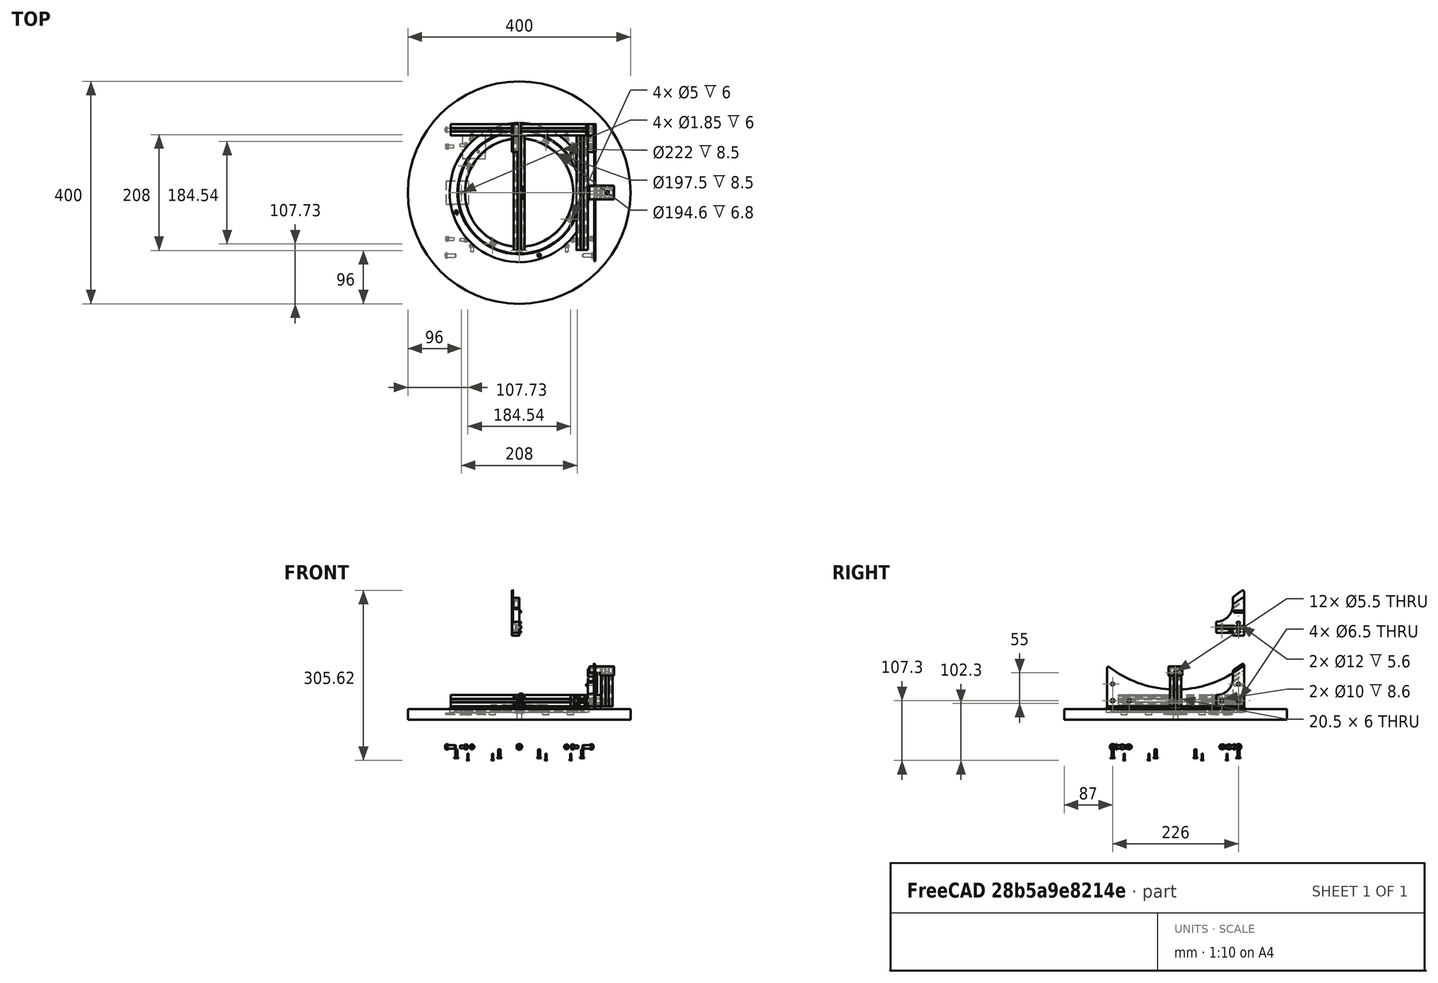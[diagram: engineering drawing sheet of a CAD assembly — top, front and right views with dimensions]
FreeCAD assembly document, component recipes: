
FREECAD ASSEMBLY — COMPONENT RECIPES ("Base")

This assembly document has 22 components, labeled P0..P21 below (a component is one placed body or linked part). 20 of them carry a construction recipe — the FreeCAD feature program that regenerates the part from scratch, quoted from this document or its linked companion documents; the rest are supplied as boundary geometry only. No exploded tour is included for this assembly.
NOTE — document 2 of 2 of this assembly tour. The two overview renders and the header above are repeated from document 1; the component sections below continue where the previous document stopped.
COMPONENT P13 — recipe-attached ("SideGuardPostA", modeled in this document).
Construction recipe (the document's own serialized feature program — sketch geometry with constraints, then the solid features built on it; lengths are millimeters unless a unit is written):

FEATURE [PartDesign::Plane] DatumPlane054  label="SideGuardPost_DatumPlane_Outer"
  AttachmentOffset = pos=(0,0,11) rot=(0,0,1;0rad)
  Length = 171.251
  MapMode = 5
  Placement = pos=(11,-2.4e-15,2.4e-15) rot=(0.57735,0.57735,0.57735;2.0944rad)
  ResizeMode = 0
  Support = -> [YZ_Plane125]
  Width = 114.566
  expr: .AttachmentOffset.Base.z = <<Common>>#<<Parameters>>.rail_width + 1
FEATURE [PartDesign::ShapeBinder] ShapeBinder015  label="SideGuardPost_ShapeBinder_Rocker"
  Support = -> [Binder]
  TraceSupport = false
FEATURE [PartDesign::Line] DatumLine004  label="SideGuardPost_DatumLine_RockerPivot"
  AttacherType = Attacher::AttachEngineLine
  Length = 20
  MapMode = 19
  Placement = pos=(0,0,215) rot=(0.57735,0.57735,0.57735;2.0944rad)
  ResizeMode = 0
  Support = -> [ShapeBinder015]
FEATURE [Sketcher::SketchObject] Sketch338  label="SideGuardPost_Block_Sketch"
  ExternalGeometry = -> [ShapeBinder015]
  FullyConstrained = true
  MapMode = 5
  Placement = pos=(0,0,0) rot=(0.57735,0.57735,0.57735;2.0944rad)
  Support = -> [YZ_Plane125]
  sketch-geometry (21):
    g0: LineSegment StartX=123 StartY=-14 StartZ=0 EndX=123 EndY=50.2697 EndZ=0
    g1: LineSegment StartX=73 StartY=-10 StartZ=0 EndX=73 EndY=10 EndZ=0
    g2: ArcOfCircle CenterX=120.5 CenterY=50.2697 CenterZ=0 NormalX=0 NormalY=0 NormalZ=1 AngleXU=0 Radius=2.5 StartAngle=1e-15 EndAngle=2.17123
    g3: Circle CenterX=113 CenterY=30 CenterZ=0 NormalX=0 NormalY=0 NormalZ=1 AngleXU=0 Radius=2.75
    g4: Circle CenterX=83 CenterY=0 CenterZ=0 NormalX=0 NormalY=0 NormalZ=1 AngleXU=0 Radius=2.75
    g5: Circle CenterX=113 CenterY=0 CenterZ=0 NormalX=0 NormalY=0 NormalZ=1 AngleXU=0 Radius=3.25
    g6: ArcOfCircle CenterX=73 CenterY=40 CenterZ=0 NormalX=0 NormalY=0 NormalZ=1 AngleXU=0 Radius=30 StartAngle=4.71239 EndAngle=6.28313
    g7: ArcOfCircle CenterX=105.5 CenterY=39.9981 CenterZ=0 NormalX=0 NormalY=0 NormalZ=1 AngleXU=0 Radius=2.5 StartAngle=2.17123 EndAngle=3.14153
    g8: LineSegment StartX=0 StartY=215 StartZ=0 EndX=113 EndY=49.9818 EndZ=0
    g9: LineSegment StartX=103 StartY=43.1341 StartZ=0 EndX=123 EndY=56.8295 EndZ=0
    g10: LineSegment StartX=113 StartY=49.9818 StartZ=0 EndX=113.847 EndY=48.7442 EndZ=0
    g11: LineSegment StartX=104.087 StartY=42.0608 StartZ=0 EndX=119.087 EndY=52.3324 EndZ=0
    g12: LineSegment StartX=103 StartY=39.9982 StartZ=0 EndX=103 EndY=43.1341 EndZ=0
    g13: LineSegment StartX=123 StartY=56.8295 StartZ=0 EndX=123 EndY=50.2697 EndZ=0
    g14: LineSegment StartX=122 StartY=-15 StartZ=0 EndX=104 EndY=-15 EndZ=0
    g15: LineSegment StartX=103 StartY=-14 StartZ=0 EndX=103 EndY=-6 EndZ=0
    g16: ArcOfCircle CenterX=104 CenterY=-14 CenterZ=0 NormalX=0 NormalY=0 NormalZ=1 AngleXU=0 Radius=1 StartAngle=3.14159 EndAngle=4.71239
    g17: ArcOfCircle CenterX=122 CenterY=-14 CenterZ=0 NormalX=0 NormalY=0 NormalZ=1 AngleXU=0 Radius=1 StartAngle=4.71239 EndAngle=6.28319
    g18: LineSegment StartX=93 StartY=-10 StartZ=0 EndX=73 EndY=-10 EndZ=0
    g19: LineSegment StartX=103 StartY=-6 StartZ=0 EndX=97 EndY=-6 EndZ=0
    g20: LineSegment StartX=97 StartY=-6 StartZ=0 EndX=93 EndY=-10 EndZ=0
  constraints (57):
    c: Vertical(g0)
    c: Coincident(g1,g18)
    c: Vertical(g1)
    c: Tangent(g0,g2) = -1.5708
    c: Coincident(g3,g-5)
    c: PointOnObject(g4,g-1)
    c: Coincident(g5,g-6)
    c: Diameter(g5) = 6.5
    c: Diameter(g3) = 5.5
    c: Equal(g3,g4)
    c: DistanceX(g4,g5) = 30
    c: DistanceX(g18,g4) = 10
    c: Radius(g2) = 2.5
    c: DistanceY(g1,g1) = 20
    c: Coincident(g6,g1)
    c: Equal(g7,g2)
    c: PointOnObject(g6,g1)
    c: Tangent(g7,g6) = 1.5708
    c: PointOnObject(g8,g-3)
    c: PointOnObject(g8,g-6)
    c: DistanceX(g9,g9) = 20
    c: PointOnObject(g8,g9)
    c: Coincident(g10,g8)
    c: PointOnObject(g10,g11)
    c: Parallel(g10,g8)
    c: Perpendicular(g11,g10)
    c: Tangent(g11,g2) = 1.5708
    c: Tangent(g11,g7) = 1.5708
    c: Distance(g10) = 1.5
    c: Coincident(g8,g-3)
    c: Coincident(g12,g6)
    c: Coincident(g12,g9)
    c: Vertical(g12)
    c: Coincident(g13,g9)
    c: Coincident(g13,g0)
    c: Vertical(g13)
    c: Perpendicular(g8,g9)
    c: Coincident(g15,g19)
    c: Horizontal(g14)
    c: Vertical(g15)
    c: Tangent(g15,g16) = 1.5708
    c: Tangent(g14,g16) = 1.5708
    c: Tangent(g0,g17) = -1.5708
    c: Tangent(g14,g17) = 1.5708
    c: Equal(g17,g16)
    c: Radius(g17) = 1
    c: DistanceX(g19,g5) = 10
    c: DistanceX(g5,g0) = 10
    c: Coincident(g20,g18)
    c: Horizontal(g18)
    c: Coincident(g19,g20)
    c: Horizontal(g19)
    c: DistanceY(g14,g18) = 5
    c: DistanceY(g18,g5) = 10
    c: DistanceX(g19,g19) = 6
    c: DistanceY(g20,g20) = 4
    c: Angle(g20,g19) = 2.35619
FEATURE [PartDesign::Pad] Pad093  label="SideGuardPost_Block"
  Direction = (1,-2e-16,3e-16)
  Length = 11
  Length2 = 10
  Placement = pos=(0,0,0) rot=(0.57735,0.57735,0.57735;2.0944rad)
  Profile = -> Sketch338
  ReferenceAxis = -> Sketch338 [N_Axis]
  Type = 0
  expr: Length = <<Common>>#<<Parameters>>.rail_width + 1
FEATURE [PartDesign::Plane] DatumPlane053  label="SideGuardPost_DatumPlane_Channel"
  AttachmentOffset = pos=(0,0,0) rot=(1,0,0;1.5708rad)
  Length = 67.8305
  MapMode = 13
  Placement = pos=(3.66667,114.087,48.9085) rot=(0,0.88459,-0.466369;3.14159rad)
  ResizeMode = 0
  Support = -> [Pad093]
  Width = 176.794
FEATURE [Sketcher::SketchObject] Sketch337  label="SideGuardPost_Plate_Sketch"
  ExternalGeometry = -> [ShapeBinder015,Sketch338]
  FullyConstrained = true
  MapMode = 5
  Placement = pos=(11,-2.4e-15,2.4e-15) rot=(0.57735,0.57735,0.57735;2.0944rad)
  Support = -> [DatumPlane054]
  expr: Constraints[2] = <<Common>>#<<Parameters>>.pri_fillet
  sketch-geometry (19):
    g0: LineSegment StartX=103 StartY=-10 StartZ=0 EndX=73 EndY=-10 EndZ=0
    g1: LineSegment StartX=0 StartY=215 StartZ=0 EndX=122.939 EndY=57.2468 EndZ=0
    g2: GeomPoint X=118.942 Y=65.7703 Z=0
    g3: Circle CenterX=113 CenterY=1.13e-14 CenterZ=0 NormalX=0 NormalY=0 NormalZ=1 AngleXU=0 Radius=3.25
    g4: ArcOfCircle CenterX=105.5 CenterY=52.9914 CenterZ=0 NormalX=0 NormalY=0 NormalZ=1 AngleXU=0 Radius=2.5 StartAngle=2.14801 EndAngle=3.14159
    g5: ArcOfCircle CenterX=120.5 CenterY=63.8154 CenterZ=0 NormalX=0 NormalY=0 NormalZ=1 AngleXU=0 Radius=2.5 StartAngle=-9e-16 EndAngle=2.24373
    g6: LineSegment StartX=123 StartY=63.8154 StartZ=0 EndX=123 EndY=-14 EndZ=0
    g7: LineSegment StartX=73 StartY=-10 StartZ=0 EndX=73 EndY=10 EndZ=0
    g8: ArcOfCircle CenterX=0 CenterY=215 CenterZ=0 NormalX=0 NormalY=0 NormalZ=1 AngleXU=0 Radius=190.831 StartAngle=5.28961 EndAngle=5.38532
    g9: LineSegment StartX=103 StartY=52.9914 StartZ=0 EndX=103 EndY=39.9982 EndZ=0
    g10: ArcOfCircle CenterX=73.0018 CenterY=39.9982 CenterZ=0 NormalX=0 NormalY=0 NormalZ=1 AngleXU=0 Radius=29.9982 StartAngle=4.71233 EndAngle=6.28319
    g11: GeomPoint X=117.303 Y=64.4786 Z=0
    g12: Circle CenterX=113 CenterY=70 CenterZ=0 NormalX=0 NormalY=0 NormalZ=1 AngleXU=0 Radius=6
    g13: LineSegment StartX=103 StartY=-10 StartZ=0 EndX=103 EndY=-14 EndZ=0
    g14: LineSegment StartX=104 StartY=-15 StartZ=0 EndX=122 EndY=-15 EndZ=0
    g15: ArcOfCircle CenterX=104 CenterY=-14 CenterZ=0 NormalX=0 NormalY=0 NormalZ=1 AngleXU=0 Radius=1 StartAngle=3.14159 EndAngle=4.71239
    g16: ArcOfCircle CenterX=122 CenterY=-14 CenterZ=0 NormalX=0 NormalY=0 NormalZ=1 AngleXU=0 Radius=1 StartAngle=4.71239 EndAngle=6.28319
    g17: LineSegment StartX=122 StartY=-14 StartZ=0 EndX=122 EndY=-15 EndZ=0
    g18: LineSegment StartX=104 StartY=-14 StartZ=0 EndX=104 EndY=-15 EndZ=0
  constraints (44):
    c: Diameter(g3) = 6.5
    c: Equal(g5,g4)
    c: Radius(g5) = 2.5
    c: Vertical(g6)
    c: Tangent(g5,g6) = 1.5708
    c: Coincident(g8,g1)
    c: Tangent(g8,g5) = 1.5708
    c: Tangent(g8,g4) = 1.5708
    c: PointOnObject(g1,g-3)
    c: Coincident(g2,g5)
    c: Vertical(g9)
    c: Tangent(g9,g4) = -1.5708
    c: Tangent(g10,g9) = 1.5708
    c: Coincident(g8,g-3)
    c: Coincident(g3,g-4)
    c: PointOnObject(g-4,g1)
    c: PointOnObject(g11,g1)
    c: PointOnObject(g11,g8)
    c: Distance(g11,g-4) = 7
    c: Coincident(g12,g-4)
    c: Diameter(g12) = 12
    c: Horizontal(g14)
    c: Coincident(g0,g13)
    c: Coincident(g7,g0)
    c: Coincident(g7,g10)
    c: Coincident(g7,g-5)
    c: Coincident(g0,g-5)
    c: Coincident(g15,g13)
    c: Coincident(g16,g-6)
    c: Coincident(g16,g6)
    c: Coincident(g14,g16)
    c: Coincident(g15,g14)
    c: Equal(g15,g16)
    c: Coincident(g6,g-6)
    c: Coincident(g17,g16)
    c: Coincident(g17,g14)
    c: Coincident(g18,g15)
    c: Coincident(g18,g14)
    c: Vertical(g18)
    c: Vertical(g17)
    c: Coincident(g9,g-7)
    c: Horizontal(g0)
    c: Vertical(g13)
    c: Coincident(g13,g-8)
FEATURE [PartDesign::Pad] Pad094  label="SideGuardPost_Plate"
  BaseFeature = -> Pad093
  Direction = (1,-1e-16,1e-16)
  Length = 2
  Length2 = 10
  Placement = pos=(0,0,0) rot=(0.57735,0.57735,0.57735;2.0944rad)
  Profile = -> Sketch337
  ReferenceAxis = -> Sketch337 [N_Axis]
  Type = 0
  expr: Length = Common#<<Parameters>>.rocker_plate
FEATURE [Sketcher::SketchObject] Sketch339  label="SideGuardPost_SideRail_Sketch"
  ExternalGeometry = -> [ShapeBinder015]
  FullyConstrained = true
  MapMode = 5
  Placement = pos=(0,0,0) rot=(-0.57735,0.57735,0.57735;4.18879rad)
  Support = -> [YZ_Plane125]
  sketch-geometry (22):
    g0: LineSegment StartX=-88 StartY=3 StartZ=0 EndX=-106 EndY=3 EndZ=0
    g1: LineSegment StartX=-106 StartY=3 StartZ=0 EndX=-106 EndY=-3 EndZ=0
    g2: LineSegment StartX=-106 StartY=-3 StartZ=0 EndX=-88 EndY=-3 EndZ=0
    g3: LineSegment StartX=-88 StartY=-3 StartZ=0 EndX=-88 EndY=3 EndZ=0
    g4: LineSegment StartX=-73 StartY=3 StartZ=0 EndX=-78 EndY=3 EndZ=0
    g5: LineSegment StartX=-78 StartY=3 StartZ=0 EndX=-78 EndY=-3 EndZ=0
    g6: LineSegment StartX=-78 StartY=-3 StartZ=0 EndX=-73 EndY=-3 EndZ=0
    g7: LineSegment StartX=-73 StartY=-3 StartZ=0 EndX=-73 EndY=3 EndZ=0
    g8: LineSegment StartX=-88 StartY=0 StartZ=0 EndX=-83 EndY=0 EndZ=0
    g9: LineSegment StartX=-83 StartY=0 StartZ=0 EndX=-78 EndY=0 EndZ=0
    g10: LineSegment StartX=-123 StartY=3 StartZ=0 EndX=-120 EndY=3 EndZ=0
    g11: LineSegment StartX=-120 StartY=3 StartZ=0 EndX=-120 EndY=-3 EndZ=0
    g12: LineSegment StartX=-120 StartY=-3 StartZ=0 EndX=-123 EndY=-3 EndZ=0
    g13: LineSegment StartX=-123 StartY=-3 StartZ=0 EndX=-123 EndY=3 EndZ=0
    g14: LineSegment StartX=-116 StartY=10 StartZ=0 EndX=-110 EndY=10 EndZ=0
    g15: LineSegment StartX=-110 StartY=10 StartZ=0 EndX=-110 EndY=7 EndZ=0
    g16: LineSegment StartX=-110 StartY=7 StartZ=0 EndX=-116 EndY=7 EndZ=0
    g17: LineSegment StartX=-116 StartY=7 StartZ=0 EndX=-116 EndY=10 EndZ=0
    g18: LineSegment StartX=-116 StartY=-7 StartZ=0 EndX=-110 EndY=-7 EndZ=0
    g19: LineSegment StartX=-110 StartY=-7 StartZ=0 EndX=-110 EndY=-10 EndZ=0
    g20: LineSegment StartX=-110 StartY=-10 StartZ=0 EndX=-116 EndY=-10 EndZ=0
    g21: LineSegment StartX=-116 StartY=-10 StartZ=0 EndX=-116 EndY=-7 EndZ=0
  constraints (63):
    c: DistanceX(g-3,g8) = 30
    c: Coincident(g0,g1)
    c: Coincident(g2,g1)
    c: Coincident(g3,g2)
    c: Coincident(g0,g3)
    c: PointOnObject(g8,g3)
    c: Coincident(g8,g9)
    c: Coincident(g5,g6)
    c: Coincident(g6,g7)
    c: Coincident(g4,g7)
    c: Coincident(g4,g5)
    c: Equal(g8,g9)
    c: PointOnObject(g9,g5)
    c: Symmetric(g4,g6,g-1)
    c: DistanceY(g7,g7) = 6
    c: Vertical(g3)
    c: Vertical(g1)
    c: Coincident(g10,g11)
    c: Coincident(g11,g12)
    c: Coincident(g12,g13)
    c: Coincident(g13,g10)
    c: Horizontal(g10)
    c: Horizontal(g12)
    c: Vertical(g11)
    c: Vertical(g13)
    c: Coincident(g14,g15)
    c: Coincident(g15,g16)
    c: Coincident(g16,g17)
    c: Coincident(g17,g14)
    c: Horizontal(g16)
    c: Vertical(g15)
    c: Vertical(g17)
    c: Coincident(g18,g19)
    c: Coincident(g19,g20)
    c: Coincident(g20,g21)
    c: Coincident(g21,g18)
    c: Horizontal(g18)
    c: Horizontal(g20)
    c: Vertical(g19)
    c: Vertical(g21)
    c: Horizontal(g2)
    c: Horizontal(g0)
    c: Horizontal(g8)
    c: Horizontal(g9)
    c: PointOnObject(g9,g-1)
    c: Vertical(g5)
    c: Horizontal(g4)
    c: Horizontal(g6)
    c: Equal(g14,g13)
    c: Equal(g13,g20)
    c: Equal(g20,g3)
    c: Equal(g3,g7)
    c: DistanceX(g8,g4) = 10
    c: Equal(g12,g19)
    c: Equal(g19,g17)
    c: Symmetric(g14,g14,g-4)
    c: Symmetric(g14,g19,g-1)
    c: DistanceY(g20,g14) = 20
    c: PointOnObject(g4,g0)
    c: DistanceX(g10,g-4) = 10
    c: DistanceX(g8,g9) = 10
    c: Symmetric(g0,g10,g-4)
    c: DistanceY(g15,g15) = 3
FEATURE [PartDesign::Pad] Pad095  label="SideGuardPost_SideRail"
  BaseFeature = -> Pad094
  Direction = (-1,2e-16,-3e-16)
  Length = 3
  Length2 = 10
  Placement = pos=(0,0,0) rot=(0.57735,0.57735,0.57735;2.0944rad)
  Profile = -> Sketch339
  ReferenceAxis = -> Sketch339 [N_Axis]
  Type = 0
FEATURE [Sketcher::SketchObject] Sketch340  label="SideGuardPost_SideBolt_Sketch"
  AttachmentOffset = pos=(0,0,2) rot=(0,0,1;0rad)
  ExternalGeometry = -> [ShapeBinder015]
  FullyConstrained = true
  MapMode = 5
  Placement = pos=(13,-2.7e-15,2.7e-15) rot=(0.57735,0.57735,0.57735;2.0944rad)
  Support = -> [DatumPlane054]
  expr: .AttachmentOffset.Base.z = <<Common>>#<<Parameters>>.rocker_plate
  sketch-geometry (2):
    g0: Circle CenterX=83 CenterY=0 CenterZ=0 NormalX=0 NormalY=0 NormalZ=1 AngleXU=0 Radius=2.75
    g1: Circle CenterX=113 CenterY=0 CenterZ=0 NormalX=0 NormalY=0 NormalZ=1 AngleXU=0 Radius=3.25
  constraints (5):
    c: PointOnObject(g0,g-1)
    c: Diameter(g0) = 5.5
    c: Coincident(g1,g-3)
    c: Diameter(g1) = 6.5
    c: DistanceX(g0,g1) = 30
FEATURE [Sketcher::SketchObject] Sketch341  label="SideGuardPost_CounterBoreSide_Sketch"
  AttachmentOffset = pos=(0,0,2) rot=(0,0,1;0rad)
  ExternalGeometry = -> [Sketch340]
  FullyConstrained = true
  MapMode = 5
  Placement = pos=(13,-2.7e-15,2.7e-15) rot=(0.57735,0.57735,0.57735;2.0944rad)
  Support = -> [DatumPlane054]
  expr: .AttachmentOffset.Base.z = <<Common>>#<<Parameters>>.rocker_plate
  sketch-geometry (1):
    g0: Circle CenterX=83 CenterY=-9.3e-15 CenterZ=0 NormalX=0 NormalY=0 NormalZ=1 AngleXU=0 Radius=5
  constraints (2):
    c: Diameter(g0) = 10
    c: Coincident(g0,g-3)
FEATURE [Sketcher::SketchObject] Sketch342  label="SideGuardPost_CBSSupport_Sketch"
  AttachmentOffset = pos=(0,0,-7) rot=(0,0,1;0rad)
  ExternalGeometry = -> [Sketch340,Sketch341]
  FullyConstrained = true
  MapMode = 5
  Placement = pos=(4,-1.7e-15,1.7e-15) rot=(0.57735,0.57735,0.57735;2.0944rad)
  Support = -> [DatumPlane054]
  expr: .AttachmentOffset.Base.z = -(<<Common>>#<<Parameters>>.rail_width + 1 - 4)
  sketch-geometry (12):
    g0: LineSegment StartX=78.8242 StartY=2.75 StartZ=0 EndX=87.1758 EndY=2.75 EndZ=0
    g1: LineSegment StartX=87.4695 StartY=2.24137 StartZ=0 EndX=83.2937 EndY=-4.99137 EndZ=0
    g2: LineSegment StartX=82.7063 StartY=-4.99137 StartZ=0 EndX=78.5305 EndY=2.24137 EndZ=0
    g3: ArcOfCircle CenterX=83 CenterY=-9.2e-15 CenterZ=0 NormalX=0 NormalY=0 NormalZ=1 AngleXU=0 Radius=5 StartAngle=2.55923 EndAngle=2.67676
    g4: ArcOfCircle CenterX=83 CenterY=-9.2e-15 CenterZ=0 NormalX=0 NormalY=0 NormalZ=1 AngleXU=0 Radius=5 StartAngle=0.464833 EndAngle=0.582364
    g5: ArcOfCircle CenterX=83 CenterY=-9.2e-15 CenterZ=0 NormalX=0 NormalY=0 NormalZ=1 AngleXU=0 Radius=5 StartAngle=4.65362 EndAngle=4.77115
    g6: LineSegment StartX=83 StartY=-9.2e-15 StartZ=0 EndX=83 EndY=2.75 EndZ=0
    g7: LineSegment StartX=83 StartY=-9.2e-15 StartZ=0 EndX=85.3816 EndY=-1.375 EndZ=0
    g8: LineSegment StartX=83 StartY=-9.2e-15 StartZ=0 EndX=80.6184 EndY=-1.375 EndZ=0
    g9: LineSegment StartX=85.3816 StartY=-1.375 StartZ=0 EndX=80.6184 EndY=-1.375 EndZ=0
    g10: LineSegment StartX=80.6184 StartY=-1.375 StartZ=0 EndX=83 EndY=2.75 EndZ=0
    g11: LineSegment StartX=83 StartY=2.75 StartZ=0 EndX=85.3816 EndY=-1.375 EndZ=0
  constraints (33):
    c: Horizontal(g0)
    c: Coincident(g3,g2)
    c: Coincident(g3,g0)
    c: Coincident(g4,g3)
    c: Coincident(g4,g0)
    c: Coincident(g4,g1)
    c: Coincident(g5,g3)
    c: Coincident(g5,g1)
    c: Coincident(g5,g2)
    c: Coincident(g6,g3)
    c: PointOnObject(g6,g0)
    c: Vertical(g6)
    c: Coincident(g7,g3)
    c: Coincident(g8,g3)
    c: PointOnObject(g8,g2)
    c: Coincident(g9,g7)
    c: Coincident(g9,g8)
    c: Coincident(g10,g8)
    c: Coincident(g10,g6)
    c: Coincident(g11,g6)
    c: Coincident(g11,g7)
    c: Horizontal(g9)
    c: Equal(g11,g9)
    c: Perpendicular(g2,g8)
    c: Perpendicular(g1,g7)
    c: Equal(g10,g11)
    c: PointOnObject(g7,g1)
    c: PointOnObject(g0,g-4)
    c: PointOnObject(g2,g-4)
    c: PointOnObject(g0,g-4)
    c: PointOnObject(g6,g-3)
    c: PointOnObject(g7,g-3)
    c: Coincident(g3,g-4)
FEATURE [Sketcher::SketchObject] Sketch343  label="SideGuardPost_Channel_Sketch"
  ExternalGeometry = -> [Pad093]
  FullyConstrained = true
  MapMode = 5
  Placement = pos=(3.66667,114.087,48.9085) rot=(0,0.88459,-0.466369;3.14159rad)
  Support = -> [DatumPlane053]
  sketch-geometry (6):
    g0: LineSegment StartX=-4.63333 StartY=6.6 StartZ=0 EndX=0.966667 EndY=6.6 EndZ=0
    g1: LineSegment StartX=0.966667 StartY=6.6 StartZ=0 EndX=0.966667 EndY=5 EndZ=0
    g2: LineSegment StartX=0.966667 StartY=5 StartZ=0 EndX=-4.63333 EndY=5 EndZ=0
    g3: LineSegment StartX=-4.63333 StartY=5 StartZ=0 EndX=-4.63333 EndY=6.6 EndZ=0
    g4: LineSegment StartX=-4.63333 StartY=5 StartZ=0 EndX=-7.33333 EndY=5 EndZ=0
    g5: LineSegment StartX=0.966667 StartY=5 StartZ=0 EndX=3.66667 EndY=5 EndZ=0
  constraints (18):
    c: Coincident(g0,g1)
    c: Coincident(g1,g2)
    c: Coincident(g2,g3)
    c: Coincident(g3,g0)
    c: Horizontal(g0)
    c: Horizontal(g2)
    c: Vertical(g1)
    c: Vertical(g3)
    c: Coincident(g4,g2)
    c: Horizontal(g4)
    c: Coincident(g5,g1)
    c: Horizontal(g5)
    c: Equal(g4,g5)
    c: DistanceX(g2,g2) = 5.6
    c: DistanceY(g1,g1) = 1.6
    c: DistanceY(g-1,g1) = 5
    c: PointOnObject(g4,g-4)
    c: PointOnObject(g5,g-5)
FEATURE [Sketcher::SketchObject] Sketch344  label="SideGuardPost_UpperCatch_Sketch"
  ExternalGeometry = -> [ShapeBinder015]
  FullyConstrained = true
  MapMode = 5
  Placement = pos=(0,0,0) rot=(0.57735,0.57735,0.57735;2.0944rad)
  Support = -> [YZ_Plane125]
  sketch-geometry (4):
    g0: LineSegment StartX=105 StartY=30 StartZ=0 EndX=121 EndY=30 EndZ=0
    g1: LineSegment StartX=121 StartY=30 StartZ=0 EndX=121 EndY=26 EndZ=0
    g2: LineSegment StartX=121 StartY=26 StartZ=0 EndX=105 EndY=26 EndZ=0
    g3: LineSegment StartX=105 StartY=26 StartZ=0 EndX=105 EndY=30 EndZ=0
  constraints (11):
    c: Coincident(g0,g1)
    c: Coincident(g1,g2)
    c: Coincident(g2,g3)
    c: Coincident(g3,g0)
    c: Horizontal(g2)
    c: Vertical(g1)
    c: Vertical(g3)
    c: Symmetric(g0,g0,g-4)
    c: DistanceY(g1,g1) = 4
    c: DistanceX(g2,g2) = 16
    c: PointOnObject(g-3,g0)
FEATURE [PartDesign::Pad] Pad096  label="SideGuardPost_Catch"
  BaseFeature = -> Pad095
  Direction = (1,-2e-16,3e-16)
  Length = 3
  Length2 = 10
  Placement = pos=(0,0,0) rot=(0.57735,0.57735,0.57735;2.0944rad)
  Profile = -> Sketch344
  ReferenceAxis = -> Sketch344 [N_Axis]
  Reversed = true
  Type = 0
FEATURE [Sketcher::SketchObject] Sketch347  label="SideGuardPost_CornerBolt_Sketch"
  AttachmentOffset = pos=(0,0,2) rot=(0,0,1;0rad)
  ExternalGeometry = -> [ShapeBinder015]
  FullyConstrained = true
  MapMode = 5
  Placement = pos=(13,-2.7e-15,2.7e-15) rot=(0.57735,0.57735,0.57735;2.0944rad)
  Support = -> [DatumPlane054]
  expr: .AttachmentOffset.Base.z = <<Common>>#<<Parameters>>.rocker_plate
  sketch-geometry (1):
    g0: Circle CenterX=113 CenterY=0 CenterZ=0 NormalX=0 NormalY=0 NormalZ=1 AngleXU=0 Radius=3.25
  constraints (2):
    c: Coincident(g0,g-3)
    c: Diameter(g0) = 6.5
FEATURE [Sketcher::SketchObject] Sketch345  label="SideGuardPost_CounterBoreCorner_Sketch"
  AttachmentOffset = pos=(0,0,2) rot=(0,0,1;0rad)
  ExternalGeometry = -> [Sketch347]
  FullyConstrained = true
  MapMode = 5
  Placement = pos=(13,-2.7e-15,2.7e-15) rot=(0.57735,0.57735,0.57735;2.0944rad)
  Support = -> [DatumPlane054]
  expr: .AttachmentOffset.Base.z = <<Common>>#<<Parameters>>.rocker_plate
  sketch-geometry (1):
    g0: Circle CenterX=113 CenterY=-1.25e-14 CenterZ=0 NormalX=0 NormalY=0 NormalZ=1 AngleXU=0 Radius=6
  constraints (2):
    c: Diameter(g0) = 12
    c: Coincident(g0,g-3)
FEATURE [Sketcher::SketchObject] Sketch346  label="SideGuardPost_CBCSupport_Sketch"
  AttachmentOffset = pos=(0,0,-4) rot=(0,0,1;0rad)
  ExternalGeometry = -> [Sketch347,Sketch345]
  FullyConstrained = true
  MapMode = 5
  Placement = pos=(7,-2e-15,2e-15) rot=(0.57735,0.57735,0.57735;2.0944rad)
  Support = -> [DatumPlane054]
  expr: .AttachmentOffset.Base.z = <<Common>>#<<Parameters>>.rocker_plate - 6
  sketch-geometry (12):
    g0: LineSegment StartX=107.956 StartY=3.25 StartZ=0 EndX=118.044 EndY=3.25 EndZ=0
    g1: LineSegment StartX=118.336 StartY=2.74285 StartZ=0 EndX=113.293 EndY=-5.99285 EndZ=0
    g2: LineSegment StartX=112.707 StartY=-5.99285 StartZ=0 EndX=107.664 EndY=2.74285 EndZ=0
    g3: ArcOfCircle CenterX=113 CenterY=-2.51e-14 CenterZ=0 NormalX=0 NormalY=0 NormalZ=1 AngleXU=0 Radius=6 StartAngle=2.56917 EndAngle=2.66681
    g4: ArcOfCircle CenterX=113 CenterY=-2.51e-14 CenterZ=0 NormalX=0 NormalY=0 NormalZ=1 AngleXU=0 Radius=6 StartAngle=0.474779 EndAngle=0.572419
    g5: ArcOfCircle CenterX=113 CenterY=-2.51e-14 CenterZ=0 NormalX=0 NormalY=0 NormalZ=1 AngleXU=0 Radius=6 StartAngle=4.66357 EndAngle=4.76121
    g6: LineSegment StartX=113 StartY=-2.51e-14 StartZ=0 EndX=113 EndY=3.25 EndZ=0
    g7: LineSegment StartX=113 StartY=-2.51e-14 StartZ=0 EndX=110.185 EndY=-1.625 EndZ=0
    g8: LineSegment StartX=113 StartY=-2.51e-14 StartZ=0 EndX=115.815 EndY=-1.625 EndZ=0
    g9: LineSegment StartX=115.815 StartY=-1.625 StartZ=0 EndX=110.185 EndY=-1.625 EndZ=0
    g10: LineSegment StartX=110.185 StartY=-1.625 StartZ=0 EndX=113 EndY=3.25 EndZ=0
    g11: LineSegment StartX=113 StartY=3.25 StartZ=0 EndX=115.815 EndY=-1.625 EndZ=0
  constraints (33):
    c: Horizontal(g0)
    c: Coincident(g3,g2)
    c: Coincident(g3,g0)
    c: Coincident(g4,g3)
    c: Coincident(g4,g0)
    c: Coincident(g4,g1)
    c: Coincident(g5,g3)
    c: Coincident(g5,g1)
    c: Coincident(g5,g2)
    c: Coincident(g6,g3)
    c: PointOnObject(g6,g0)
    c: Vertical(g6)
    c: Coincident(g7,g3)
    c: PointOnObject(g7,g2)
    c: Coincident(g8,g3)
    c: PointOnObject(g8,g1)
    c: Coincident(g9,g8)
    c: Coincident(g9,g7)
    c: Perpendicular(g2,g7)
    c: Perpendicular(g1,g8)
    c: Coincident(g10,g7)
    c: Coincident(g10,g6)
    c: Coincident(g11,g6)
    c: Coincident(g11,g8)
    c: Equal(g10,g11)
    c: Equal(g11,g9)
    c: Horizontal(g9)
    c: PointOnObject(g0,g-4)
    c: PointOnObject(g2,g-4)
    c: PointOnObject(g1,g-4)
    c: Coincident(g3,g-4)
    c: PointOnObject(g8,g-3)
    c: PointOnObject(g6,g-3)
FEATURE [PartDesign::Pocket] Pocket196  label="SideGuardPost_Channel"
  BaseFeature = -> Pad096
  Direction = (0,0.825091,0.565)
  Length = 5
  Length2 = 5
  Midplane = true
  Placement = pos=(0,0,0) rot=(0.57735,0.57735,0.57735;2.0944rad)
  Profile = -> Sketch343
  ReferenceAxis = -> Sketch343 [N_Axis]
  Type = 1
FEATURE [Sketcher::SketchObject] Sketch348  label="SideGuardPost_LowerChannel_Sketch"
  AttachmentOffset = pos=(0,0,123) rot=(0,0,1;0rad)
  FullyConstrained = true
  MapMode = 5
  Placement = pos=(0,123,2.73e-14) rot=(0,0.707107,0.707107;3.14159rad)
  Support = -> [XZ_Plane124]
  expr: .AttachmentOffset.Base.z = <<Common>>#<<Parameters>>.boxsize_y / 2
  expr: Constraints[12] = <<Common>>#<<Parameters>>.rail_width + 1
  sketch-geometry (7):
    g0: LineSegment StartX=-2.7 StartY=-8.4 StartZ=0 EndX=-8.3 EndY=-8.4 EndZ=0
    g1: LineSegment StartX=-8.3 StartY=-8.4 StartZ=0 EndX=-8.3 EndY=-10 EndZ=0
    g2: LineSegment StartX=-8.3 StartY=-10 StartZ=0 EndX=-2.7 EndY=-10 EndZ=0
    g3: LineSegment StartX=-2.7 StartY=-10 StartZ=0 EndX=-2.7 EndY=-8.4 EndZ=0
    g4: LineSegment StartX=-11 StartY=0 StartZ=0 EndX=-11 EndY=-10 EndZ=0
    g5: LineSegment StartX=-11 StartY=-10 StartZ=0 EndX=-8.3 EndY=-10 EndZ=0
    g6: LineSegment StartX=-2.7 StartY=-10 StartZ=0 EndX=0 EndY=-10 EndZ=0
  constraints (21):
    c: Coincident(g0,g1)
    c: Coincident(g1,g2)
    c: Coincident(g2,g3)
    c: Coincident(g3,g0)
    c: Horizontal(g0)
    c: Horizontal(g2)
    c: Vertical(g1)
    c: Vertical(g3)
    c: PointOnObject(g4,g-1)
    c: Vertical(g4)
    c: DistanceX(g2,g2) = 5.6
    c: DistanceY(g1,g1) = 1.6
    c: DistanceX(g4,g-1) = 11
    c: Coincident(g5,g4)
    c: Coincident(g5,g1)
    c: Coincident(g6,g2)
    c: PointOnObject(g6,g-2)
    c: Horizontal(g6)
    c: Horizontal(g5)
    c: Equal(g5,g6)
    c: DistanceY(g6,g-1) = 10
FEATURE [PartDesign::Pocket] Pocket197  label="SideGuardPost_LowerChannel"
  BaseFeature = -> Pocket196
  Direction = (0,-1,-2e-16)
  Length = 5
  Length2 = 5
  Placement = pos=(0,0,0) rot=(0.57735,0.57735,0.57735;2.0944rad)
  Profile = -> Sketch348
  ReferenceAxis = -> Sketch348 [N_Axis]
  Type = 2
FEATURE [PartDesign::Pocket] Pocket198  label="SideGuardPost_CornerBolt"
  BaseFeature = -> Pocket197
  Direction = (-1,1e-16,-1e-16)
  Length = 5
  Length2 = 5
  Placement = pos=(0,0,0) rot=(0.57735,0.57735,0.57735;2.0944rad)
  Profile = -> Sketch347
  ReferenceAxis = -> Sketch347 [N_Axis]
  Type = 1
FEATURE [PartDesign::Pocket] Pocket199  label="SideGuardPost_SideBolt"
  BaseFeature = -> Pocket198
  Direction = (-1,1e-16,-1e-16)
  Length = 5
  Length2 = 5
  Placement = pos=(0,0,0) rot=(0.57735,0.57735,0.57735;2.0944rad)
  Profile = -> Sketch340
  ReferenceAxis = -> Sketch340 [N_Axis]
  Type = 1
FEATURE [PartDesign::Pocket] Pocket200  label="SideGuardPost_CounterBoreCorner"
  BaseFeature = -> Pocket199
  Direction = (-1,1e-16,-1e-16)
  Length = 6
  Length2 = 5
  Placement = pos=(0,0,0) rot=(0.57735,0.57735,0.57735;2.0944rad)
  Profile = -> Sketch345
  ReferenceAxis = -> Sketch345 [N_Axis]
  Type = 0
FEATURE [PartDesign::Pocket] Pocket201  label="SideGuardPost_CounterBoreSide"
  BaseFeature = -> Pocket200
  Direction = (-1,1e-16,-1e-16)
  Length = 9
  Length2 = 5
  Placement = pos=(0,0,0) rot=(0.57735,0.57735,0.57735;2.0944rad)
  Profile = -> Sketch341
  ReferenceAxis = -> Sketch341 [N_Axis]
  Type = 0
  expr: Length = <<Common>>#<<Parameters>>.rail_width + 1 + <<Common>>#<<Parameters>>.rocker_plate - 4
FEATURE [PartDesign::Pocket] Pocket202  label="SideGuardPost_CBCSupport"
  BaseFeature = -> Pocket201
  Direction = (-1,1e-16,-1e-16)
  Length = 0.2
  Length2 = 5
  Placement = pos=(0,0,0) rot=(0.57735,0.57735,0.57735;2.0944rad)
  Profile = -> Sketch346
  ReferenceAxis = -> Sketch346 [N_Axis]
  Type = 0
FEATURE [PartDesign::Pocket] Pocket203  label="SideGuardPost_CBSSupport"
  BaseFeature = -> Pocket202
  Direction = (-1,1e-16,-1e-16)
  Length = 0.2
  Length2 = 5
  Placement = pos=(0,0,0) rot=(0.57735,0.57735,0.57735;2.0944rad)
  Profile = -> Sketch342
  ReferenceAxis = -> Sketch342 [N_Axis]
  Type = 0
FEATURE [PartDesign::Chamfer] Chamfer004  label="SideGuardPost_Chamfer"
  Angle = 45
  Base = -> Pocket203 [Face51]
  BaseFeature = -> Pocket203
  ChamferType = 0
  FlipDirection = false
  Placement = pos=(0,0,0) rot=(0.57735,0.57735,0.57735;2.0944rad)
  Size = 0.4
  Size2 = 1
  SupportTransform = false
  UseAllEdges = false
FEATURE [PartDesign::CoordinateSystem] Local_CS258  label="LCS_SideGuardPostA_Corner"
  AttacherType = Attacher::AttachEngine3D
  MapMode = 11
  Placement = pos=(1.78e-14,113,-3.93e-14) rot=(0.707107,0,0.707107;3.14159rad)
  Support = -> [Chamfer004]
FEATURE [PartDesign::CoordinateSystem] Local_CS259  label="LCS_SideGuardPostA_Side"
  AttacherType = Attacher::AttachEngine3D
  AttachmentOffset = pos=(0,0,0) rot=(0,0,1;1.5708rad)
  MapMode = 11
  Placement = pos=(-3.55e-14,83,-2.93e-14) rot=(0.57735,-0.57735,0.57735;4.18879rad)
  Support = -> [Chamfer004]
FEATURE [PartDesign::Body] Body022070  label="SideGuardPostA"
  Group = -> [ShapeBinder015,Sketch338,Sketch339,Sketch337,DatumLine004,DatumPlane053,Pad093,Pad094,Pad095,Sketch340,Sketch341,Sketch342,DatumPlane054,Sketch343,Sketch344,Sketch345,Sketch346,Pad096,Sketch347,Pocket196,Sketch348,Pocket197,Pocket198,Pocket199,Pocket200,Pocket201,Pocket202,Pocket203,Chamfer004,Local_CS258,Local_CS259]
  Origin = -> Origin124
  Placement = pos=(123,0,-132) rot=(0,0,1;0rad)
  Tip = -> Chamfer004
  expr: .Placement.Base.x = <<Common>>#<<Parameters>>.boxsize_x / 2
  expr: .Placement.Base.z = <<Common>>#<<Parameters>>.datum_azbase
COMPONENT P14 — geometry summary ("SideGuardPostB"; no construction recipe available for this part):
  bounding box: 81.3 x 50.0 x 16.0 mm
  tessellated surface: 3,632 triangles
  volume: 25453 mm^3 (39% of its bounding box)
COMPONENT P15 — recipe-attached ("BaseWheelBlockSB", modeled in this document).
Construction recipe (the document's own serialized feature program — sketch geometry with constraints, then the solid features built on it; lengths are millimeters unless a unit is written):

FEATURE [Sketcher::SketchObject] Sketch350  label="BaseWheelBlockSB_Body_Sketch"
  FullyConstrained = true
  MapMode = 5
  Support = -> [XY_Plane128]
  expr: Constraints[22] = <<Common>>#<<Parameters>>.bolt_y - 10 - 30
  expr: Constraints[32] = <<Common>>#<<Parameters>>.bolt_x - 10
  sketch-geometry (23):
    g0: ArcOfCircle CenterX=0 CenterY=0 CenterZ=0 NormalX=0 NormalY=0 NormalZ=1 AngleXU=0 Radius=104.75 StartAngle=0 EndAngle=1.5708
    g1: LineSegment StartX=88.1276 StartY=63.0542 StartZ=0 EndX=99.4503 EndY=43.0343 EndZ=0
    g2: LineSegment StartX=99.4503 StartY=43.0343 StartZ=0 EndX=93.3573 EndY=39.5883 EndZ=0
    g3: LineSegment StartX=93.3573 StartY=39.5883 StartZ=0 EndX=82.0346 EndY=59.6082 EndZ=0
    g4: LineSegment StartX=82.0346 StartY=59.6082 StartZ=0 EndX=88.1276 EndY=63.0542 EndZ=0
    g5: LineSegment StartX=91.1777 StartY=51.5674 StartZ=0 EndX=0 EndY=0 EndZ=0
    g6: LineSegment StartX=92 StartY=73 StartZ=0 EndX=103 EndY=73 EndZ=0
    g7: LineSegment StartX=103 StartY=73 StartZ=0 EndX=103 EndY=46.5731 EndZ=0
    g8: LineSegment StartX=92 StartY=58.2387 StartZ=0 EndX=92 EndY=73 EndZ=0
    g9: GeomPoint X=93.789 Y=53.0443 Z=0
    g10: GeomPoint X=94.6594 Y=53.5366 Z=0
    g11: LineSegment StartX=98.5977 StartY=46.5731 StartZ=0 EndX=92 EndY=58.2387 EndZ=0
    g12: LineSegment StartX=98.5977 StartY=46.5731 StartZ=0 EndX=103 EndY=46.5731 EndZ=0
    g13: GeomPoint X=87.6959 Y=49.5982 Z=0
    g14: LineSegment StartX=103 StartY=68 StartZ=0 EndX=99 EndY=68 EndZ=0
    g15: LineSegment StartX=99 StartY=68 StartZ=0 EndX=99 EndY=70.5 EndZ=0
    g16: LineSegment StartX=99 StartY=70.5 StartZ=0 EndX=85.0654 EndY=70.5 EndZ=0
    g17: LineSegment StartX=103 StartY=63 StartZ=0 EndX=99 EndY=63 EndZ=0
    g18: LineSegment StartX=99 StartY=63 StartZ=0 EndX=99 EndY=60.5 EndZ=0
    g19: LineSegment StartX=99 StartY=60.5 StartZ=0 EndX=90.7211 EndY=60.5 EndZ=0
    g20: LineSegment StartX=96.1363 StartY=50.9253 StartZ=0 EndX=100.488 EndY=53.3867 EndZ=0
    g21: LineSegment StartX=93.1825 StartY=56.1478 StartZ=0 EndX=97.5347 EndY=58.6093 EndZ=0
    g22: LineSegment StartX=97.5347 StartY=58.6093 StartZ=0 EndX=100.488 EndY=53.3867 EndZ=0
  constraints (70):
    c: Coincident(g0,g-1)
    c: PointOnObject(g0,g-2)
    c: PointOnObject(g0,g-1)
    c: DistanceY(g0) = 104.75
    c: Coincident(g2,g1)
    c: Coincident(g3,g2)
    c: Coincident(g4,g3)
    c: Coincident(g4,g1)
    c: PointOnObject(g5,g0)
    c: Coincident(g5,g0)
    c: Parallel(g2,g4)
    c: Parallel(g4,g5)
    c: Symmetric(g3,g2,g5)
    c: Parallel(g1,g3)
    c: Distance(g3) = 23
    c: Distance(g4) = 7
    c: Horizontal(g6)
    c: Coincident(g7,g6)
    c: Vertical(g7)
    c: Coincident(g8,g11)
    c: Coincident(g8,g6)
    c: Vertical(g8)
    c: DistanceY(g6) = 73
    c: PointOnObject(g9,g1)
    c: PointOnObject(g10,g5)
    c: PointOnObject(g9,g5)
    c: Distance(g9,g10) = 1
    c: Parallel(g11,g1)
    c: PointOnObject(g10,g11)
    c: Coincident(g12,g11)
    c: Coincident(g12,g7)
    c: Horizontal(g12)
    c: DistanceX(g6) = 103
    c: PointOnObject(g13,g3)
    c: PointOnObject(g13,g5)
    c: Distance(g13,g5) = 4
    c: PointOnObject(g14,g7)
    c: Horizontal(g14)
    c: Coincident(g15,g14)
    c: Vertical(g15)
    c: Coincident(g16,g15)
    c: Horizontal(g16)
    c: PointOnObject(g17,g7)
    c: Horizontal(g17)
    c: Coincident(g18,g17)
    c: Vertical(g18)
    c: Coincident(g19,g18)
    c: PointOnObject(g19,g11)
    c: Horizontal(g19)
    c: PointOnObject(g16,g11)
    c: Equal(g15,g18)
    c: Equal(g17,g14)
    c: DistanceY(g17,g14) = 5
    c: Distance(g10,g11) = 8
    c: Distance(g19,g10) = 8
    c: DistanceX(g14,g14) = 4
    c: DistanceX(g19,g19) = 8.27893
    c: DistanceY(g15,g6) = 2.5
    c: DistanceY(g18,g15) = 10
    c: PointOnObject(g20,g11)
    c: PointOnObject(g21,g11)
    c: Coincident(g22,g21)
    c: Coincident(g22,g20)
    c: Perpendicular(g11,g20)
    c: Perpendicular(g11,g21)
    c: Symmetric(g20,g21,g5)
    c: Distance(g22) = 6
    c: Distance(g20) = 5
    c: DistanceX(g8,g18) = 7
    c: DistanceY(g18,g6) = 12.5
FEATURE [PartDesign::Pad] Pad097  label="BaseWheelBlockSB_Body"
  Direction = (0,0,1)
  Length = 20
  Length2 = 10
  Midplane = true
  Profile = -> Sketch350
  ReferenceAxis = -> Sketch350 [N_Axis]
  Type = 0
FEATURE [Sketcher::SketchObject] Sketch351  label="BaseWheelBlockSB_Tab_Sketch"
  ExternalGeometry = -> [Sketch350]
  FullyConstrained = true
  MapMode = 5
  Support = -> [XY_Plane128]
  sketch-geometry (8):
    g0: LineSegment StartX=103 StartY=46.5731 StartZ=0 EndX=106 EndY=46.5731 EndZ=0
    g1: LineSegment StartX=106 StartY=46.5731 StartZ=0 EndX=106 EndY=57.5 EndZ=0
    g2: LineSegment StartX=106 StartY=57.5 StartZ=0 EndX=103 EndY=60.5 EndZ=0
    g3: LineSegment StartX=103 StartY=60.5 StartZ=0 EndX=103 EndY=46.5731 EndZ=0
    g4: LineSegment StartX=103 StartY=73 StartZ=0 EndX=106 EndY=73 EndZ=0
    g5: LineSegment StartX=106 StartY=73 StartZ=0 EndX=106 EndY=70.6 EndZ=0
    g6: LineSegment StartX=106 StartY=70.6 StartZ=0 EndX=103 EndY=70.6 EndZ=0
    g7: LineSegment StartX=103 StartY=70.6 StartZ=0 EndX=103 EndY=73 EndZ=0
  constraints (22):
    c: Coincident(g0,g1)
    c: Coincident(g1,g2)
    c: Coincident(g2,g3)
    c: Coincident(g3,g0)
    c: Horizontal(g0)
    c: Vertical(g1)
    c: Vertical(g3)
    c: Coincident(g0,g-3)
    c: Angle(g2,g1) = 2.35619
    c: DistanceX(g0,g0) = 3
    c: DistanceY(g2,g-4) = 12.5
    c: Coincident(g4,g5)
    c: Coincident(g5,g6)
    c: Coincident(g6,g7)
    c: Coincident(g7,g4)
    c: Horizontal(g4)
    c: Horizontal(g6)
    c: Vertical(g5)
    c: Vertical(g7)
    c: Coincident(g4,g-4)
    c: PointOnObject(g5,g1)
    c: DistanceY(g5,g5) = 2.4
FEATURE [PartDesign::Pad] Pad098  label="BaseWheelBlockSB_Tab"
  BaseFeature = -> Pad097
  Direction = (0,0,1)
  Length = 6
  Length2 = 10
  Midplane = true
  Profile = -> Sketch351
  ReferenceAxis = -> Sketch351 [N_Axis]
  Type = 0
FEATURE [Sketcher::SketchObject] Sketch354  label="BaseWheelBlockSB_MountHole_Sketch"
  ExternalGeometry = -> [Pad098]
  FullyConstrained = true
  MapMode = 5
  Placement = pos=(92,0,0) rot=(0.57735,-0.57735,-0.57735;2.0944rad)
  Support = -> [Pad098]
  sketch-geometry (1):
    g0: Circle CenterX=-65.5 CenterY=0 CenterZ=0 NormalX=0 NormalY=0 NormalZ=1 AngleXU=0 Radius=2.5
  constraints (3):
    c: PointOnObject(g0,g-1)
    c: Diameter(g0) = 5
    c: DistanceX(g-3,g0) = 7.5
FEATURE [PartDesign::Hole] Hole  label="BaseWheelBlockSB_MountHole"
  BaseFeature = -> Pad098
  CustomThreadClearance = 0
  Depth = 72.6746
  DepthType = 1
  Diameter = 5.5
  DrillForDepth = false
  DrillPoint = 1
  DrillPointAngle = 118
  HoleCutCountersinkAngle = 90
  HoleCutCustomValues = false
  HoleCutDepth = 5.4
  HoleCutDiameter = 10
  HoleCutType = 4
  ModelThread = false
  Profile = -> Sketch354
  Tapered = false
  TaperedAngle = 90
  ThreadClass = 0
  ThreadDepth = 72.6746
  ThreadDepthType = 0
  ThreadDirection = 0
  ThreadFit = 0
  ThreadSize = 13
  ThreadType = 1
  Threaded = false
  UseCustomThreadClearance = false
FEATURE [Sketcher::SketchObject] Sketch355  label="BaseWheelBlockSB_BearingHole_Sketch"
  ExternalGeometry = -> [Pad098]
  FullyConstrained = true
  MapMode = 5
  Placement = pos=(94.6594,53.5366,0) rot=(0.771415,-0.449955,-0.449955;1.82746rad)
  Support = -> [Pad098]
  sketch-geometry (1):
    g0: Circle CenterX=5.3e-15 CenterY=0 CenterZ=0 NormalX=0 NormalY=0 NormalZ=1 AngleXU=0 Radius=2
  constraints (3):
    c: DistanceX(g0,g-3) = 8
    c: Diameter(g0) = 4
    c: DistanceY(g0,g-1) = 0
FEATURE [PartDesign::Hole] Hole041  label="BaseWheelBlockSB_BearingHole"
  BaseFeature = -> Hole
  CustomThreadClearance = 0
  Depth = 7
  DepthType = 0
  Diameter = 4.5
  DrillForDepth = false
  DrillPoint = 1
  DrillPointAngle = 118
  HoleCutCountersinkAngle = 90
  HoleCutCustomValues = false
  HoleCutDepth = 4
  HoleCutDiameter = 5.6
  HoleCutType = 1
  ModelThread = false
  Profile = -> Sketch355
  Tapered = false
  TaperedAngle = 90
  ThreadClass = 0
  ThreadDepth = 7
  ThreadDepthType = 0
  ThreadDirection = 0
  ThreadFit = 0
  ThreadSize = 11
  ThreadType = 1
  Threaded = false
  UseCustomThreadClearance = false
  expr: HoleCutDiameter = <<Common>>#<<Parameters>>.acc_M4Bore
FEATURE [PartDesign::Chamfer] Chamfer006  label="BaseWheelBlockSB_Chamfer"
  Angle = 45
  Base = -> Hole041 [Face6,Edge29,Face5,Edge1,Edge19,Edge6,Edge5,Edge24,Edge23]
  BaseFeature = -> Hole041
  ChamferType = 0
  FlipDirection = false
  Size = 0.4
  Size2 = 1
  SupportTransform = false
  UseAllEdges = false
FEATURE [PartDesign::CoordinateSystem] Local_CS262  label="LCS_BaseWheelBlockSB_MountHole"
  AttacherType = Attacher::AttachEngine3D
  MapMode = 11
  Placement = pos=(97.4,65.5,0) rot=(0.57735,0.57735,-0.57735;4.18879rad)
  Support = -> [Hole041]
FEATURE [PartDesign::CoordinateSystem] Local_CS263  label="LCS_BaseWheelBlocl_SB_BearingHole"
  AttacherType = Attacher::AttachEngine3D
  MapMode = 11
  Placement = pos=(94.6594,53.5366,0) rot=(0.381288,0.653689,-0.653689;3.87014rad)
  Support = -> [Hole041]
FEATURE [PartDesign::Body] Body022073  label="BaseWheelBlockSB"
  Group = -> [Sketch350,Pad097,Sketch351,Pad098,Sketch354,Hole,Sketch355,Hole041,Chamfer006,Local_CS262,Local_CS263]
  Origin = -> Origin128
  Placement = pos=(0,0,-132) rot=(0,0,1;0rad)
  Tip = -> Chamfer006
  expr: .Placement.Base.z = <<Common>>#<<Parameters>>.datum_azbase
COMPONENT P16 — recipe-attached ("BaseWheel", modeled in this document).
Construction recipe (the document's own serialized feature program — sketch geometry with constraints, then the solid features built on it; lengths are millimeters unless a unit is written):

FEATURE [Sketcher::SketchObject] Sketch366  label="BaseWheel_Profile_Sketch"
  FullyConstrained = true
  MapMode = 5
  Support = -> [XY_Plane131]
  sketch-geometry (7):
    g0: LineSegment StartX=0 StartY=5 StartZ=0 EndX=0 EndY=12.5 EndZ=0
    g1: LineSegment StartX=0 StartY=12.5 StartZ=0 EndX=6 EndY=12.5 EndZ=0
    g2: LineSegment StartX=6 StartY=12.5 StartZ=0 EndX=6 EndY=5.46077 EndZ=0
    g3: LineSegment StartX=6 StartY=5.46077 StartZ=0 EndX=5.4 EndY=6.5 EndZ=0
    g4: LineSegment StartX=5.4 StartY=6.5 StartZ=0 EndX=0.6 EndY=6.5 EndZ=0
    g5: LineSegment StartX=0.6 StartY=6.5 StartZ=0 EndX=0.6 EndY=5 EndZ=0
    g6: LineSegment StartX=0.6 StartY=5 StartZ=0 EndX=0 EndY=5 EndZ=0
  constraints (21):
    c: PointOnObject(g0,g-2)
    c: Coincident(g1,g0)
    c: Horizontal(g1)
    c: Coincident(g2,g1)
    c: Vertical(g2)
    c: Coincident(g3,g2)
    c: Coincident(g4,g3)
    c: Horizontal(g4)
    c: Coincident(g5,g4)
    c: Vertical(g5)
    c: Coincident(g6,g5)
    c: Coincident(g6,g0)
    c: Vertical(g0)
    c: Horizontal(g6)
    c: DistanceX(g6,g6) = 0.6
    c: DistanceY(g4) = 6.5
    c: DistanceY(g5) = 5
    c: Angle(g4,g3) = 2.0944
    c: DistanceY(g0) = 12.5
    c: DistanceX(g3,g3) = 0.6
    c: DistanceX(g4,g2) = 5.4
FEATURE [PartDesign::Revolution] Revolution  label="BaseWheel_Revolution"
  Angle = 360
  Axis = (1,0,0)
  Base = (0,0,0)
  Profile = -> Sketch366
  ReferenceAxis = -> X_Axis131
FEATURE [PartDesign::CoordinateSystem] Local_CS264  label="LCS_BaseWheel_BearingSide"
  AttacherType = Attacher::AttachEngine3D
  MapMode = 11
  Placement = pos=(6,0,0) rot=(0.707107,0,0.707107;3.14159rad)
  Support = -> [Revolution]
FEATURE [PartDesign::Body] Body022076  label="BaseWheel"
  Group = -> [Sketch366,Revolution,Local_CS264]
  Origin = -> Origin131
  Placement = pos=(0,0,-132) rot=(0,0,1;0rad)
  Tip = -> Revolution
  expr: .Placement.Base.z = <<Common>>#<<Parameters>>.datum_azbase
COMPONENT P17 — recipe-attached ("BasePadSide", modeled in this document).
Construction recipe (the document's own serialized feature program — sketch geometry with constraints, then the solid features built on it; lengths are millimeters unless a unit is written):

FEATURE [Sketcher::SketchObject] Sketch367  label="BasePadSide_Body_Sketch"
  FullyConstrained = true
  MapMode = 5
  Support = -> [XY_Plane117]
  expr: Constraints[19] = <<Common>>#<<Parameters>>.pri_fillet
  sketch-geometry (17):
    g0: Circle CenterX=-104 CenterY=0 CenterZ=0 NormalX=0 NormalY=0 NormalZ=1 AngleXU=0 Radius=2.5
    g1: ArcOfCircle CenterX=-130.75 CenterY=19.5 CenterZ=0 NormalX=0 NormalY=0 NormalZ=1 AngleXU=0 Radius=1.25 StartAngle=1.5708 EndAngle=3.14159
    g2: LineSegment StartX=-130.75 StartY=20.75 StartZ=0 EndX=-91.75 EndY=20.75 EndZ=0
    g3: ArcOfCircle CenterX=-91.75 CenterY=19.5 CenterZ=0 NormalX=0 NormalY=0 NormalZ=1 AngleXU=0 Radius=1.25 StartAngle=5.8458e-12 EndAngle=1.5708
    g4: LineSegment StartX=-90.5 StartY=19.5 StartZ=0 EndX=-90.5 EndY=-19.5 EndZ=0
    g5: ArcOfCircle CenterX=-91.75 CenterY=-19.5 CenterZ=0 NormalX=0 NormalY=0 NormalZ=1 AngleXU=0 Radius=1.25 StartAngle=4.71239 EndAngle=6.28319
    g6: LineSegment StartX=-91.75 StartY=-20.75 StartZ=0 EndX=-130.75 EndY=-20.75 EndZ=0
    g7: ArcOfCircle CenterX=-130.75 CenterY=-19.5 CenterZ=0 NormalX=0 NormalY=0 NormalZ=1 AngleXU=0 Radius=1.25 StartAngle=3.14159 EndAngle=4.71239
    g8: LineSegment StartX=-132 StartY=-19.5 StartZ=0 EndX=-132 EndY=19.5 EndZ=0
    g9: LineSegment StartX=-104 StartY=0 StartZ=0 EndX=0 EndY=0 EndZ=0
    g10: Circle CenterX=-118.5 CenterY=0 CenterZ=0 NormalX=0 NormalY=0 NormalZ=1 AngleXU=0 Radius=2.5
    g11: Circle CenterX=-104 CenterY=0 CenterZ=0 NormalX=0 NormalY=0 NormalZ=1 AngleXU=0 Radius=1
    g12: LineSegment StartX=-130.75 StartY=19.5 StartZ=0 EndX=-91.75 EndY=-19.5 EndZ=0
    g13: LineSegment StartX=-91.75 StartY=19.5 StartZ=0 EndX=-130.75 EndY=-19.5 EndZ=0
    g14: GeomPoint X=-111.25 Y=0 Z=0
    g15: LineSegment StartX=-118.5 StartY=0 StartZ=0 EndX=-111.25 EndY=0 EndZ=0
    g16: LineSegment StartX=-111.25 StartY=0 StartZ=0 EndX=-104 EndY=0 EndZ=0
  constraints (40):
    c: Distance(g-1,g0) = 104
    c: Diameter(g0) = 5
    c: Tangent(g1,g2) = 1.5708
    c: Tangent(g2,g3) = 1.5708
    c: Tangent(g3,g4) = 1.5708
    c: Tangent(g4,g5) = 1.5708
    c: Tangent(g5,g6) = 1.5708
    c: Tangent(g6,g7) = 1.5708
    c: Tangent(g7,g8) = 1.5708
    c: Tangent(g8,g1) = 1.5708
    c: Horizontal(g2)
    c: Horizontal(g6)
    c: Vertical(g4)
    c: Vertical(g8)
    c: Equal(g1,g3)
    c: Equal(g3,g5)
    c: Equal(g5,g7)
    c: Equal(g2,g8)
    c: Coincident(g9,g0)
    c: Diameter(g3) = 2.5
    c: DistanceX(g2,g2) = 39
    c: Coincident(g9,g-1)
    c: Equal(g10,g0)
    c: PointOnObject(g10,g9)
    c: Distance(g10,g9) = 118.5
    c: Coincident(g11,g0)
    c: Diameter(g11) = 2
    c: Coincident(g12,g1)
    c: Coincident(g12,g5)
    c: Coincident(g13,g3)
    c: Coincident(g13,g7)
    c: PointOnObject(g14,g12)
    c: PointOnObject(g14,g13)
    c: PointOnObject(g14,g9)
    c: Coincident(g15,g10)
    c: Coincident(g15,g14)
    c: Coincident(g16,g14)
    c: Coincident(g16,g11)
    c: Equal(g16,g15)
    c: Horizontal(g9)
FEATURE [PartDesign::Pad] Pad104  label="BasePadSide_Body"
  Direction = (0,0,1)
  Length = 2
  Length2 = 4
  Profile = -> Sketch367
  ReferenceAxis = -> Sketch367 [N_Axis]
  Type = 4
FEATURE [Sketcher::SketchObject] Sketch368  label="BasePadSide_Pillar_Sketch"
  ExternalGeometry = -> [Sketch367]
  FullyConstrained = true
  MapMode = 5
  Support = -> [XY_Plane117]
  sketch-geometry (2):
    g0: Circle CenterX=-104 CenterY=0 CenterZ=0 NormalX=0 NormalY=0 NormalZ=1 AngleXU=0 Radius=2.35
    g1: Circle CenterX=-104 CenterY=0 CenterZ=0 NormalX=0 NormalY=0 NormalZ=1 AngleXU=0 Radius=1.1
  constraints (4):
    c: Diameter(g0) = 4.7
    c: Coincident(g1,g0)
    c: Diameter(g1) = 2.2
    c: Coincident(g-3,g0)
FEATURE [Sketcher::SketchObject] Sketch369  label="BasePadSide_Hole_Sketch"
  FullyConstrained = true
  MapMode = 5
  Support = -> [XY_Plane117]
  sketch-geometry (2):
    g0: LineSegment StartX=0 StartY=0 StartZ=0 EndX=-73.5391 EndY=73.5391 EndZ=0
    g1: Circle CenterX=-73.5391 CenterY=73.5391 CenterZ=0 NormalX=0 NormalY=0 NormalZ=1 AngleXU=0 Radius=1
  constraints (5):
    c: Coincident(g0,g-1)
    c: Distance(g0) = 104
    c: Angle(g0) = 2.35619
    c: Coincident(g1,g0)
    c: Diameter(g1) = 2
FEATURE [Sketcher::SketchObject] Sketch370  label="BasePadSide_Cut_Sketch"
  FullyConstrained = true
  MapMode = 5
  Placement = pos=(0,0,0) rot=(1,0,0;1.5708rad)
  Support = -> [XZ_Plane117]
  sketch-geometry (18):
    g0: LineSegment StartX=-96.7 StartY=7 StartZ=0 EndX=-2.84e-14 EndY=7 EndZ=0
    g1: LineSegment StartX=-96.7 StartY=7 StartZ=0 EndX=-96.7 EndY=3 EndZ=0
    g2: LineSegment StartX=-93.7 StartY=3.6e-15 StartZ=0 EndX=-2.84e-14 EndY=3.6e-15 EndZ=0
    g3: LineSegment StartX=-2.84e-14 StartY=3.6e-15 StartZ=0 EndX=-2.84e-14 EndY=7 EndZ=0
    g4: ArcOfCircle CenterX=-93.7 CenterY=3 CenterZ=0 NormalX=0 NormalY=0 NormalZ=1 AngleXU=0 Radius=3 StartAngle=3.14159 EndAngle=4.71239
    g5: LineSegment StartX=-96.7 StartY=3 StartZ=0 EndX=-93.7 EndY=3 EndZ=0
    g6: LineSegment StartX=-93.7 StartY=3 StartZ=0 EndX=-93.7 EndY=3.6e-15 EndZ=0
    g7: LineSegment StartX=-165 StartY=7 StartZ=0 EndX=-98.5 EndY=7 EndZ=0
    g8: LineSegment StartX=-98.5 StartY=7 StartZ=0 EndX=-98.5 EndY=1.8e-15 EndZ=0
    g9: LineSegment StartX=-165 StartY=1.6e-15 StartZ=0 EndX=-165 EndY=7 EndZ=0
    g10: LineSegment StartX=-145.5 StartY=1.6e-15 StartZ=0 EndX=-165 EndY=1.6e-15 EndZ=0
    g11: LineSegment StartX=-98.5 StartY=1.6e-15 StartZ=0 EndX=-110 EndY=1.6e-15 EndZ=0
    g12: LineSegment StartX=-144.1 StartY=-1.4 StartZ=0 EndX=-145.5 EndY=1.6e-15 EndZ=0
    g13: LineSegment StartX=-110 StartY=1.6e-15 StartZ=0 EndX=-111.4 EndY=-1.4 EndZ=0
    g14: LineSegment StartX=-111.4 StartY=-1.4 StartZ=0 EndX=-144.1 EndY=-1.4 EndZ=0
    g15: GeomPoint X=-118.5 Y=1.6e-15 Z=0
    g16: LineSegment StartX=-145.5 StartY=1.6e-15 StartZ=0 EndX=-118.5 EndY=1.6e-15 EndZ=0
    g17: LineSegment StartX=-118.5 StartY=1.6e-15 StartZ=0 EndX=-110 EndY=1.6e-15 EndZ=0
  constraints (49):
    c: Horizontal(g0)
    c: Coincident(g1,g0)
    c: Vertical(g1)
    c: Horizontal(g2)
    c: Coincident(g3,g2)
    c: Coincident(g3,g0)
    c: Vertical(g3)
    c: Coincident(g4,g1)
    c: Coincident(g4,g2)
    c: Coincident(g5,g1)
    c: Coincident(g5,g4)
    c: Coincident(g6,g4)
    c: Coincident(g6,g2)
    c: Coincident(g7,g8)
    c: Coincident(g10,g9)
    c: Coincident(g9,g7)
    c: Horizontal(g7)
    c: Vertical(g8)
    c: Vertical(g9)
    c: Horizontal(g5)
    c: Vertical(g6)
    c: PointOnObject(g7,g0)
    c: DistanceY(g0) = 7
    c: Coincident(g2,g-1)
    c: DistanceY(g6,g6) = 3
    c: PointOnObject(g11,g-1)
    c: DistanceX(g7,g2) = 165
    c: DistanceX(g7,g2) = 98.5
    c: DistanceX(g7,g0) = 1.8
    c: Coincident(g11,g8)
    c: Coincident(g12,g10)
    c: Horizontal(g10)
    c: Coincident(g11,g13)
    c: Horizontal(g11)
    c: Coincident(g14,g12)
    c: Coincident(g13,g14)
    c: Horizontal(g14)
    c: DistanceY(g13,g13) = 1.4
    c: Coincident(g16,g10)
    c: Coincident(g16,g15)
    c: Coincident(g17,g15)
    c: Coincident(g17,g11)
    c: Horizontal(g17)
    c: Horizontal(g16)
    c: DistanceX(g15,g-1) = 118.5
    c: DistanceX(g15,g11) = 8.5
    c: DistanceX(g10,g2) = 145.5
    c: Angle(g14,g12) = 2.35619
    c: Angle(g13,g14) = 2.35619
FEATURE [PartDesign::Groove] Groove009  label="BasePadSide_Groove"
  Angle = 360
  Axis = (1e-16,1e-16,1)
  Base = (0,0,0)
  BaseFeature = -> Pad104
  Profile = -> Sketch370
  ReferenceAxis = -> Z_Axis117
  Reversed = true
FEATURE [PartDesign::Pad] Pad105  label="BasePadSide_Pillar"
  BaseFeature = -> Groove009
  Direction = (0,0,1)
  Length = 2
  Length2 = 10
  Profile = -> Sketch368
  ReferenceAxis = -> Sketch368 [N_Axis]
  Type = 0
FEATURE [Sketcher::SketchObject] Sketch373  label="BasePadSide_BoltHole_Sketch"
  ExternalGeometry = -> [Pad105]
  FullyConstrained = true
  MapMode = 5
  Placement = pos=(0,0,-4) rot=(1,0,0;3.14159rad)
  Support = -> [Pad105]
  sketch-geometry (1):
    g0: Circle CenterX=-104 CenterY=0 CenterZ=0 NormalX=0 NormalY=0 NormalZ=1 AngleXU=0 Radius=2.25
  constraints (2):
    c: Coincident(g0,g-3)
    c: Diameter(g0) = 4.5
FEATURE [PartDesign::Hole] Hole046  label="BasePadSide_BoltHole"
  BaseFeature = -> Pad105
  CustomThreadClearance = 0
  Depth = 119.394
  DepthType = 1
  Diameter = 2.2
  DrillForDepth = false
  DrillPoint = 1
  DrillPointAngle = 118
  HoleCutCountersinkAngle = 90
  HoleCutCustomValues = false
  HoleCutDepth = 2.2
  HoleCutDiameter = 4.4
  HoleCutType = 1
  ModelThread = false
  Profile = -> Sketch373
  Tapered = false
  TaperedAngle = 90
  ThreadClass = 0
  ThreadDepth = 119.394
  ThreadDepthType = 0
  ThreadDirection = 0
  ThreadFit = 0
  ThreadSize = 0
  ThreadType = 0
  Threaded = false
  UseCustomThreadClearance = false
FEATURE [Sketcher::SketchObject] Sketch374  label="BasePadSide_BHSupport_Sketch"
  ExternalGeometry = -> [Hole046]
  FullyConstrained = true
  MapMode = 5
  Placement = pos=(0,0,-1.8) rot=(1,0,0;3.14159rad)
  Support = -> [Hole046]
  sketch-geometry (5):
    g0: LineSegment StartX=-102.095 StartY=1.1 StartZ=0 EndX=-104 EndY=-2.2 EndZ=0
    g1: LineSegment StartX=-104 StartY=-2.2 StartZ=0 EndX=-105.905 EndY=1.1 EndZ=0
    g2: LineSegment StartX=-105.905 StartY=1.1 StartZ=0 EndX=-102.095 EndY=1.1 EndZ=0
    g3: LineSegment StartX=-104 StartY=0 StartZ=0 EndX=-104.953 EndY=-0.55 EndZ=0
    g4: LineSegment StartX=-104 StartY=0 StartZ=0 EndX=-103.047 EndY=-0.55 EndZ=0
  constraints (15):
    c: Horizontal(g2)
    c: Equal(g2,g1)
    c: Equal(g1,g0)
    c: Coincident(g2,g1)
    c: Coincident(g0,g2)
    c: Coincident(g1,g0)
    c: Coincident(g3,g-4)
    c: PointOnObject(g3,g1)
    c: Coincident(g4,g3)
    c: PointOnObject(g4,g0)
    c: Perpendicular(g0,g4)
    c: Perpendicular(g1,g3)
    c: PointOnObject(g0,g-4)
    c: PointOnObject(g1,g-4)
    c: PointOnObject(g0,g-4)
FEATURE [PartDesign::Pocket] Pocket205  label="BasePadSide_BHSupport"
  BaseFeature = -> Hole046
  Direction = (0,0,1)
  Length = 0.2
  Length2 = 5
  Profile = -> Sketch374
  ReferenceAxis = -> Sketch374 [N_Axis]
  Type = 0
FEATURE [PartDesign::Chamfer] Chamfer009  label="BasePadSide_Chamfer"
  Angle = 45
  Base = -> Pocket205 [Face2]
  BaseFeature = -> Pocket205
  ChamferType = 0
  FlipDirection = false
  Size = 0.4
  Size2 = 1
  SupportTransform = false
  UseAllEdges = false
FEATURE [PartDesign::CoordinateSystem] Local_CS265  label="LCS_BasePadSide_MountBolt"
  AttacherType = Attacher::AttachEngine3D
  MapMode = 11
  Placement = pos=(-104,0,-1.8) rot=(0.707107,0.707107,0;3.14159rad)
  Support = -> [Hole046]
FEATURE [PartDesign::CoordinateSystem] Local_CS273  label="LCS_BasePadSide_Pillar"
  AttacherType = Attacher::AttachEngine3D
  MapMode = 11
  Placement = pos=(-104,0,0) rot=(0.707107,-0.707107,0;3.14159rad)
  Support = -> [Hole046]
FEATURE [PartDesign::Body] Body022077  label="BasePadSide"
  Group = -> [Sketch367,Sketch368,Pad104,Sketch369,Sketch370,Groove009,Pad105,Sketch373,Hole046,Sketch374,Pocket205,Chamfer009,Local_CS265,Local_CS273]
  Origin = -> Origin132
  Placement = pos=(0,0,-153) rot=(0,0,1;0rad)
  Tip = -> Chamfer009
  expr: .Placement.Base.z = <<Common>>#<<Parameters>>.datum_azbase - 10 - 11
COMPONENT P18 — recipe-attached ("BaseBearingTop", modeled in this document).
Construction recipe (the document's own serialized feature program — sketch geometry with constraints, then the solid features built on it; lengths are millimeters unless a unit is written):

FEATURE [Sketcher::SketchObject] Sketch371  label="BaseBearingTop_Profile_Sketch"
  FullyConstrained = true
  MapMode = 5
  Placement = pos=(0,0,0) rot=(1,0,0;1.5708rad)
  Support = -> [XZ_Plane132]
  sketch-geometry (6):
    g0: LineSegment StartX=-109.5 StartY=0.8 StartZ=0 EndX=-97.3 EndY=0.8 EndZ=0
    g1: LineSegment StartX=-98.5 StartY=0 StartZ=0 EndX=-109.5 EndY=0 EndZ=0
    g2: LineSegment StartX=-109.5 StartY=0 StartZ=0 EndX=-109.5 EndY=0.8 EndZ=0
    g3: LineSegment StartX=-97.3 StartY=0.8 StartZ=0 EndX=-97.3 EndY=-6 EndZ=0
    g4: LineSegment StartX=-97.3 StartY=-6 StartZ=0 EndX=-98.5 EndY=-6 EndZ=0
    g5: LineSegment StartX=-98.5 StartY=-6 StartZ=0 EndX=-98.5 EndY=0 EndZ=0
  constraints (18):
    c: Coincident(g1,g2)
    c: Coincident(g2,g0)
    c: Horizontal(g0)
    c: Horizontal(g1)
    c: Vertical(g2)
    c: Coincident(g3,g4)
    c: Coincident(g4,g5)
    c: Horizontal(g4)
    c: Vertical(g3)
    c: Vertical(g5)
    c: Coincident(g3,g0)
    c: DistanceY(g2,g2) = 0.8
    c: Coincident(g1,g5)
    c: DistanceX(g4,g4) = 1.2
    c: DistanceX(g1,g1) = 11
    c: DistanceY(g5,g5) = 6
    c: DistanceX(g1) = -98.5
    c: PointOnObject(g1,g-1)
FEATURE [PartDesign::Revolution] Revolution001  label="BaseBearingTop_Revolution"
  Angle = 360
  Axis = (1e-16,1e-16,1)
  Base = (0,0,0)
  Placement = pos=(0,0,0) rot=(1,0,0;1.5708rad)
  Profile = -> Sketch371
  ReferenceAxis = -> Z_Axis132
FEATURE [PartDesign::Line] DatumLine005  label="DatumLine_BaseBearingTop_Bolt"
  AttacherType = Attacher::AttachEngineLine
  AttachmentOffset = pos=(104,0,0) rot=(0,0,1;0rad)
  Length = 20
  MapMode = 29
  Placement = pos=(104,0,-1.15e-14) rot=(0,0,1;0rad)
  ResizeMode = 0
  Support = -> [Z_Axis132]
FEATURE [PartDesign::Plane] DatumPlane056  label="DatumPlane_BaseBearingTop_BoltCut"
  Length = 239.556
  MapMode = 3
  Placement = pos=(104,0,-1.15e-14) rot=(1,0,0;1.5708rad)
  ResizeMode = 0
  Support = -> [DatumLine005]
  Width = 70.9115
FEATURE [Sketcher::SketchObject] Sketch372  label="BaseBearingTop_BoltCut_Sketch"
  ExternalGeometry = -> [Revolution001]
  FullyConstrained = true
  MapMode = 5
  Placement = pos=(104,0,-1.15e-14) rot=(1,0,0;1.5708rad)
  Support = -> [DatumPlane056]
  sketch-geometry (5):
    g0: LineSegment StartX=2.35 StartY=-6 StartZ=0 EndX=2.35 EndY=-0.85 EndZ=0
    g1: LineSegment StartX=2.35 StartY=-0.85 StartZ=0 EndX=3.2 EndY=0 EndZ=0
    g2: LineSegment StartX=3.2 StartY=0 StartZ=0 EndX=0.925 EndY=0 EndZ=0
    g3: LineSegment StartX=0.925 StartY=0 StartZ=0 EndX=0.925 EndY=-6 EndZ=0
    g4: LineSegment StartX=0.925 StartY=-6 StartZ=0 EndX=2.35 EndY=-6 EndZ=0
  constraints (16):
    c: Vertical(g0)
    c: Coincident(g1,g0)
    c: Coincident(g2,g1)
    c: Vertical(g3)
    c: Coincident(g4,g3)
    c: Coincident(g4,g0)
    c: Horizontal(g4)
    c: DistanceX(g1) = 3.2
    c: Angle(g2,g1) = 0.785398
    c: DistanceX(g0) = 2.35
    c: Horizontal(g2)
    c: PointOnObject(g3,g-3)
    c: DistanceX(g3) = 0.925
    c: DistanceX(g4,g4) = 1.425
    c: Coincident(g2,g3)
    c: PointOnObject(g2,g-1)
FEATURE [PartDesign::Revolution] Revolution002  label="BaseBearingTop_BoltCut_Revolution"
  Angle = 360
  Axis = (1e-16,1e-16,1)
  Base = (104,0,-1.15e-14)
  BaseFeature = -> Revolution001
  Placement = pos=(0,0,0) rot=(1,0,0;1.5708rad)
  Profile = -> Sketch372
  ReferenceAxis = -> DatumLine005
  Reversed = true
FEATURE [PartDesign::PolarPattern] PolarPattern  label="BaseBearingTop_PolarPattern"
  Angle = 360
  Axis = -> Z_Axis132
  BaseFeature = -> Revolution002
  Occurrences = 4
  Originals = -> [Revolution002]
  Placement = pos=(0,0,0) rot=(1,0,0;1.5708rad)
FEATURE [PartDesign::CoordinateSystem] Local_CS266  label="LCS_BaseBearingTop_MountFlat"
  AttacherType = Attacher::AttachEngine3D
  AttachmentOffset = pos=(0,0,0) rot=(0,0,1;0.479532rad)
  MapMode = 11
  Placement = pos=(0,0,-1.22e-14) rot=(0,0,-1;1.09126rad)
  Support = -> [PolarPattern]
  expr: .AttachmentOffset.Rotation.Yaw = 45 deg - acos(<<Common>>#<<Parameters>>.bolt_y / 118.5)
FEATURE [PartDesign::Body] Body022078  label="BaseBearingTop"
  Group = -> [Sketch371,Revolution001,DatumLine005,DatumPlane056,Sketch372,Revolution002,PolarPattern,Local_CS266]
  Origin = -> Origin133
  Placement = pos=(0,0,-144.5) rot=(0,0,1;0rad)
  Tip = -> PolarPattern
  expr: .Placement.Base.z = <<Common>>#<<Parameters>>.datum_azbase - 10 - 2.5
COMPONENT P19 — recipe-attached ("AFrame_PS", modeled in this document).
Construction recipe (the document's own serialized feature program — sketch geometry with constraints, then the solid features built on it; lengths are millimeters unless a unit is written):

FEATURE [Sketcher::SketchObject] Sketch048  label="AFrame_PS_Sketch"
  FullyConstrained = true
  MapMode = 5
  Placement = pos=(0,0,0) rot=(1,0,0;1.5708rad)
  Support = -> [XZ_Plane043]
  sketch-geometry (75):
    g0: LineSegment StartX=3 StartY=10 StartZ=0 EndX=3 EndY=8 EndZ=0
    g1: LineSegment StartX=3 StartY=8 StartZ=0 EndX=6 EndY=8 EndZ=0
    g2: LineSegment StartX=2.58579 StartY=4 StartZ=0 EndX=-2.58579 EndY=4 EndZ=0
    g3: LineSegment StartX=-6 StartY=8 StartZ=0 EndX=-3 EndY=8 EndZ=0
    g4: LineSegment StartX=-3 StartY=8 StartZ=0 EndX=-3 EndY=10 EndZ=0
    g5: Circle CenterX=0 CenterY=0 CenterZ=0 NormalX=0 NormalY=0 NormalZ=1 AngleXU=0 Radius=2.1
    g6: LineSegment StartX=-10 StartY=3 StartZ=0 EndX=-8 EndY=3 EndZ=0
    g7: LineSegment StartX=-8 StartY=3 StartZ=0 EndX=-8 EndY=6 EndZ=0
    g8: LineSegment StartX=-4 StartY=2.58579 StartZ=0 EndX=-4 EndY=-2.58579 EndZ=0
    g9: LineSegment StartX=-8 StartY=-6 StartZ=0 EndX=-8 EndY=-3 EndZ=0
    g10: LineSegment StartX=-8 StartY=-3 StartZ=0 EndX=-10 EndY=-3 EndZ=0
    g11: LineSegment StartX=-3 StartY=-10 StartZ=0 EndX=-3 EndY=-8 EndZ=0
    g12: LineSegment StartX=-3 StartY=-8 StartZ=0 EndX=-6 EndY=-8 EndZ=0
    g13: LineSegment StartX=-2.58579 StartY=-4 StartZ=0 EndX=2.58579 EndY=-4 EndZ=0
    g14: LineSegment StartX=6 StartY=-8 StartZ=0 EndX=3 EndY=-8 EndZ=0
    g15: LineSegment StartX=3 StartY=-8 StartZ=0 EndX=3 EndY=-10 EndZ=0
    g16: LineSegment StartX=10 StartY=-3 StartZ=0 EndX=8 EndY=-3 EndZ=0
    g17: LineSegment StartX=8 StartY=-3 StartZ=0 EndX=8 EndY=-6 EndZ=0
    g18: LineSegment StartX=8 StartY=-6 StartZ=0 EndX=7.41421 EndY=-6 EndZ=0
    g19: LineSegment StartX=7.41421 StartY=-6 StartZ=0 EndX=4 EndY=-2.58579 EndZ=0
    g20: LineSegment StartX=4 StartY=-2.58579 StartZ=0 EndX=4 EndY=2.58579 EndZ=0
    g21: LineSegment StartX=4 StartY=2.58579 StartZ=0 EndX=7.41421 EndY=6 EndZ=0
    g22: LineSegment StartX=7.41421 StartY=6 StartZ=0 EndX=8 EndY=6 EndZ=0
    g23: LineSegment StartX=8 StartY=6 StartZ=0 EndX=8 EndY=3 EndZ=0
    g24: LineSegment StartX=8 StartY=3 StartZ=0 EndX=10 EndY=3 EndZ=0
    g25: LineSegment StartX=6 StartY=8 StartZ=0 EndX=6 EndY=7.41421 EndZ=0
    g26: LineSegment StartX=6 StartY=7.41421 StartZ=0 EndX=2.58579 EndY=4 EndZ=0
    g27: LineSegment StartX=-2.58579 StartY=4 StartZ=0 EndX=-6 EndY=7.41421 EndZ=0
    g28: LineSegment StartX=-6 StartY=7.41421 StartZ=0 EndX=-6 EndY=8 EndZ=0
    g29: LineSegment StartX=-8 StartY=6 StartZ=0 EndX=-7.41421 EndY=6 EndZ=0
    g30: LineSegment StartX=-7.41421 StartY=6 StartZ=0 EndX=-4 EndY=2.58579 EndZ=0
    g31: LineSegment StartX=-4 StartY=-2.58579 StartZ=0 EndX=-7.41421 EndY=-6 EndZ=0
    g32: LineSegment StartX=-7.41421 StartY=-6 StartZ=0 EndX=-8 EndY=-6 EndZ=0
    g33: LineSegment StartX=-2.58579 StartY=-4 StartZ=0 EndX=-6 EndY=-7.41421 EndZ=0
    g34: LineSegment StartX=-6 StartY=-7.41421 StartZ=0 EndX=-6 EndY=-8 EndZ=0
    g35: LineSegment StartX=2.58579 StartY=-4 StartZ=0 EndX=6 EndY=-7.41421 EndZ=0
    g36: LineSegment StartX=6 StartY=-7.41421 StartZ=0 EndX=6 EndY=-8 EndZ=0
    g37: LineSegment StartX=-4 StartY=2.58579 StartZ=0 EndX=-2.58579 EndY=4 EndZ=0
    g38: LineSegment StartX=-7.41421 StartY=7.41421 StartZ=0 EndX=7.41421 EndY=7.41421 EndZ=0
    g39: LineSegment StartX=7.41421 StartY=7.41421 StartZ=0 EndX=7.41421 EndY=-7.41421 EndZ=0
    g40: LineSegment StartX=7.41421 StartY=-7.41421 StartZ=0 EndX=-7.41421 EndY=-7.41421 EndZ=0
    g41: LineSegment StartX=-7.41421 StartY=-7.41421 StartZ=0 EndX=-7.41421 EndY=7.41421 EndZ=0
    g42: LineSegment StartX=-10 StartY=10 StartZ=0 EndX=10 EndY=10 EndZ=0
    g43: LineSegment StartX=10 StartY=10 StartZ=0 EndX=10 EndY=-10 EndZ=0
    g44: LineSegment StartX=10 StartY=-10 StartZ=0 EndX=-10 EndY=-10 EndZ=0
    g45: LineSegment StartX=-10 StartY=-10 StartZ=0 EndX=-10 EndY=10 EndZ=0
    g46: LineSegment StartX=4 StartY=4 StartZ=0 EndX=-4 EndY=4 EndZ=0
    g47: LineSegment StartX=-4 StartY=4 StartZ=0 EndX=-4 EndY=-4 EndZ=0
    g48: LineSegment StartX=-4 StartY=-4 StartZ=0 EndX=4 EndY=-4 EndZ=0
    g49: LineSegment StartX=4 StartY=-4 StartZ=0 EndX=4 EndY=4 EndZ=0
    g50: LineSegment StartX=-10 StartY=-10 StartZ=0 EndX=10 EndY=10 EndZ=0
    g51: LineSegment StartX=-10 StartY=10 StartZ=0 EndX=10 EndY=-10 EndZ=0
    g52: LineSegment StartX=2.58579 StartY=4 StartZ=0 EndX=4 EndY=2.58579 EndZ=0
    g53: LineSegment StartX=2.58579 StartY=-4 StartZ=0 EndX=4 EndY=-2.58579 EndZ=0
    g54: LineSegment StartX=-4 StartY=-2.58579 StartZ=0 EndX=-2.58579 EndY=-4 EndZ=0
    g55: LineSegment StartX=10 StartY=3 StartZ=0 EndX=3 EndY=10 EndZ=0
    g56: LineSegment StartX=-3 StartY=10 StartZ=0 EndX=-10 EndY=3 EndZ=0
    g57: LineSegment StartX=-10 StartY=-3 StartZ=0 EndX=-3 EndY=-10 EndZ=0
    g58: LineSegment StartX=3 StartY=-10 StartZ=0 EndX=10 EndY=-3 EndZ=0
    g59: ArcOfCircle CenterX=-9 CenterY=9 CenterZ=0 NormalX=0 NormalY=0 NormalZ=1 AngleXU=0 Radius=1 StartAngle=1.57078 EndAngle=3.14161
    g60: ArcOfCircle CenterX=9 CenterY=9 CenterZ=0 NormalX=0 NormalY=0 NormalZ=1 AngleXU=0 Radius=1 StartAngle=6.28316 EndAngle=7.854
    g61: ArcOfCircle CenterX=9 CenterY=-9 CenterZ=0 NormalX=0 NormalY=0 NormalZ=1 AngleXU=0 Radius=1 StartAngle=4.71238 EndAngle=6.28319
    g62: ArcOfCircle CenterX=-9 CenterY=-9 CenterZ=0 NormalX=0 NormalY=0 NormalZ=1 AngleXU=0 Radius=1 StartAngle=3.14159 EndAngle=4.71241
    g63: LineSegment StartX=-10 StartY=-9 StartZ=0 EndX=10 EndY=-9 EndZ=0
    g64: LineSegment StartX=-10 StartY=8.99998 StartZ=0 EndX=10 EndY=8.99998 EndZ=0
    g65: LineSegment StartX=-8.99998 StartY=10 StartZ=0 EndX=-8.99998 EndY=-10 EndZ=0
    g66: LineSegment StartX=8.99999 StartY=10 StartZ=0 EndX=8.99999 EndY=-10 EndZ=0
    g67: LineSegment StartX=-10 StartY=8.99998 StartZ=0 EndX=-10 EndY=3 EndZ=0
    g68: LineSegment StartX=-10 StartY=-3 StartZ=0 EndX=-10 EndY=-9 EndZ=0
    g69: LineSegment StartX=-8.99998 StartY=10 StartZ=0 EndX=-3 EndY=10 EndZ=0
    g70: LineSegment StartX=8.99999 StartY=10 StartZ=0 EndX=3 EndY=10 EndZ=0
    g71: LineSegment StartX=10 StartY=8.99998 StartZ=0 EndX=10 EndY=3 EndZ=0
    g72: LineSegment StartX=10 StartY=-9 StartZ=0 EndX=10 EndY=-3 EndZ=0
    g73: LineSegment StartX=8.99999 StartY=-10 StartZ=0 EndX=3 EndY=-10 EndZ=0
    g74: LineSegment StartX=-8.99998 StartY=-10 StartZ=0 EndX=-3 EndY=-10 EndZ=0
  constraints (212):
    c: Diameter(g5) = 4.2
    c: Coincident(g42,g43)
    c: Coincident(g43,g44)
    c: Coincident(g44,g45)
    c: Coincident(g45,g42)
    c: Horizontal(g44)
    c: Vertical(g45)
    c: Symmetric(g42,g43,g-1)
    c: Symmetric(g42,g42,g-2)
    c: Coincident(g5,g-1)
    c: Coincident(g38,g41)
    c: Coincident(g7,g29)
    c: Coincident(g29,g30)
    c: Coincident(g27,g28)
    c: Coincident(g3,g28)
    c: Coincident(g3,g4)
    c: Coincident(g6,g7)
    c: Coincident(g2,g27)
    c: Coincident(g2,g37)
    c: Coincident(g8,g30)
    c: Coincident(g8,g37)
    c: Coincident(g8,g31)
    c: Coincident(g13,g33)
    c: Coincident(g9,g10)
    c: Coincident(g11,g12)
    c: Coincident(g12,g34)
    c: Coincident(g33,g34)
    c: Coincident(g40,g41)
    c: Coincident(g31,g32)
    c: Coincident(g9,g32)
    c: Coincident(g14,g36)
    c: Coincident(g17,g18)
    c: Coincident(g39,g40)
    c: Coincident(g18,g19)
    c: Coincident(g35,g36)
    c: Coincident(g13,g35)
    c: Coincident(g19,g20)
    c: Coincident(g16,g17)
    c: Coincident(g0,g1)
    c: Coincident(g1,g25)
    c: Coincident(g22,g23)
    c: Coincident(g23,g24)
    c: Coincident(g21,g22)
    c: Coincident(g38,g39)
    c: Coincident(g25,g26)
    c: Coincident(g2,g26)
    c: Coincident(g20,g21)
    c: Horizontal(g1)
    c: Horizontal(g3)
    c: Horizontal(g12)
    c: Horizontal(g14)
    c: Vertical(g34)
    c: Vertical(g11)
    c: Vertical(g15)
    c: Vertical(g36)
    c: Vertical(g4)
    c: Vertical(g0)
    c: Vertical(g28)
    c: Vertical(g25)
    c: Vertical(g7)
    c: Vertical(g9)
    c: Vertical(g23)
    c: Vertical(g17)
    c: Horizontal(g29)
    c: Horizontal(g6)
    c: Horizontal(g10)
    c: Horizontal(g32)
    c: Horizontal(g22)
    c: Horizontal(g24)
    c: Horizontal(g16)
    c: Horizontal(g18)
    c: Parallel(g30,g27)
    c: Parallel(g27,g35)
    c: Parallel(g35,g19)
    c: Parallel(g21,g26)
    c: Parallel(g31,g33)
    c: Coincident(g46,g47)
    c: Coincident(g47,g48)
    c: Coincident(g48,g49)
    c: Coincident(g49,g46)
    c: Horizontal(g46)
    c: Horizontal(g48)
    c: Vertical(g47)
    c: Vertical(g49)
    c: Horizontal(g2)
    c: Horizontal(g13)
    c: Vertical(g8)
    c: Vertical(g20)
    c: PointOnObject(g2,g46)
    c: PointOnObject(g19,g49)
    c: PointOnObject(g13,g48)
    c: PointOnObject(g8,g47)
    c: Coincident(g50,g44)
    c: Coincident(g50,g42)
    c: Coincident(g51,g42)
    c: Coincident(g51,g43)
    c: PointOnObject(g39,g51)
    c: PointOnObject(g38,g50)
    c: PointOnObject(g38,g51)
    c: Vertical(g39)
    c: Vertical(g41)
    c: Horizontal(g38)
    c: Horizontal(g40)
    c: PointOnObject(g46,g50)
    c: PointOnObject(g46,g51)
    c: PointOnObject(g48,g51)
    c: Parallel(g27,g51)
    c: Parallel(g26,g50)
    c: Perpendicular(g51,g37)
    c: Parallel(g31,g26)
    c: PointOnObject(g4,g42)
    c: PointOnObject(g24,g43)
    c: PointOnObject(g6,g45)
    c: PointOnObject(g10,g45)
    c: PointOnObject(g29,g41)
    c: PointOnObject(g31,g41)
    c: PointOnObject(g33,g40)
    c: PointOnObject(g35,g40)
    c: PointOnObject(g18,g39)
    c: PointOnObject(g21,g39)
    c: PointOnObject(g25,g38)
    c: PointOnObject(g27,g38)
    c: Coincident(g52,g2)
    c: Coincident(g52,g20)
    c: Coincident(g53,g13)
    c: Coincident(g53,g19)
    c: Coincident(g54,g8)
    c: Coincident(g54,g13)
    c: Perpendicular(g50,g54)
    c: Perpendicular(g51,g53)
    c: Perpendicular(g50,g52)
    c: Equal(g37,g52)
    c: Equal(g52,g53)
    c: Equal(g53,g54)
    c: Distance(g37) = 2
    c: Coincident(g14,g15)
    c: PointOnObject(g6,g24)
    c: PointOnObject(g9,g16)
    c: PointOnObject(g11,g4)
    c: PointOnObject(g14,g0)
    c: PointOnObject(g11,g44)
    c: PointOnObject(g15,g44)
    c: DistanceX(g42) = 10
    c: DistanceY(g49,g49) = 8
    c: DistanceY(g18,g21) = 12
    c: Coincident(g56,g4)
    c: Coincident(g57,g10)
    c: Coincident(g58,g15)
    c: Perpendicular(g51,g58)
    c: Perpendicular(g50,g55)
    c: Perpendicular(g51,g56)
    c: Equal(g58,g57)
    c: Equal(g57,g55)
    c: DistanceY(g16,g24) = 6
    c: Equal(g42,g43)
    c: Coincident(g55,g0)
    c: Coincident(g55,g24)
    c: Coincident(g56,g6)
    c: Coincident(g11,g57)
    c: Coincident(g16,g58)
    c: DistanceX(g6,g6) = 2
    c: Equal(g6,g10)
    c: Equal(g10,g24)
    c: Equal(g24,g16)
    c: Equal(g16,g15)
    c: Equal(g15,g11)
    c: Equal(g11,g4)
    c: Equal(g4,g0)
    c: PointOnObject(g59,g51)
    c: PointOnObject(g59,g45)
    c: PointOnObject(g59,g42)
    c: PointOnObject(g60,g42)
    c: PointOnObject(g60,g43)
    c: PointOnObject(g61,g51)
    c: PointOnObject(g61,g43)
    c: PointOnObject(g61,g44)
    c: PointOnObject(g62,g50)
    c: PointOnObject(g62,g44)
    c: PointOnObject(g62,g45)
    c: Radius(g62) = 1
    c: Equal(g62,g59)
    c: Equal(g59,g60)
    c: Equal(g60,g61)
    c: Coincident(g63,g62)
    c: Coincident(g63,g61)
    c: Horizontal(g63)
    c: Coincident(g64,g59)
    c: Coincident(g64,g60)
    c: Horizontal(g64)
    c: Coincident(g65,g59)
    c: Coincident(g65,g62)
    c: Vertical(g65)
    c: Coincident(g66,g60)
    c: Coincident(g66,g61)
    c: Vertical(g66)
    c: PointOnObject(g62,g63)
    c: Coincident(g67,g59)
    c: Coincident(g67,g6)
    c: Coincident(g68,g10)
    c: Coincident(g68,g62)
    c: Coincident(g69,g59)
    c: Coincident(g69,g4)
    c: Coincident(g70,g60)
    c: Coincident(g70,g0)
    c: Coincident(g71,g60)
    c: Coincident(g71,g24)
    c: Coincident(g72,g61)
    c: Coincident(g72,g16)
    c: Coincident(g73,g61)
    c: Coincident(g73,g15)
    c: Coincident(g74,g62)
    c: Coincident(g74,g11)
FEATURE [PartDesign::Pad] Pad025  label="AFrame_PS_Pad"
  Direction = (0,-1,-2e-16)
  Length = 206
  Length2 = 100
  Midplane = true
  Placement = pos=(0,0,0) rot=(1,0,0;1.5708rad)
  Profile = -> Sketch048
  Type = 0
  expr: Length = <<Common>>#<<Parameters>>.boxsize_y - 40
FEATURE [PartDesign::CoordinateSystem] Local_CS104  label="LCS_AFrame_PS_Corner_FP"
  AttacherType = Attacher::AttachEngine3D
  AttachmentOffset = pos=(-10,-103,0) rot=(0,0,1;1.5708rad)
  MapMode = 5
  Placement = pos=(-10,-103,0) rot=(0,0,1;1.5708rad)
  Support = -> [XY_Plane043]
  expr: .AttachmentOffset.Base.y = -(<<Common>>#<<Parameters>>.boxsize_y / 2 - 20)
FEATURE [PartDesign::CoordinateSystem] Local_CS105  label="LCS_AFrame_PS_Corner_AP"
  AttacherType = Attacher::AttachEngine3D
  AttachmentOffset = pos=(-10,103,0) rot=(0,0,1;3.14159rad)
  MapMode = 5
  Placement = pos=(-10,103,0) rot=(0,0,1;3.14159rad)
  Support = -> [XY_Plane043]
  expr: .AttachmentOffset.Base.y = <<Common>>#<<Parameters>>.boxsize_y / 2 - 20
FEATURE [PartDesign::CoordinateSystem] Local_CS  label="LCS_AFrame_PS_Corner_FS"
  AttacherType = Attacher::AttachEngine3D
  AttachmentOffset = pos=(10,-103,0) rot=(0,0,1;0rad)
  MapMode = 5
  Placement = pos=(10,-103,0) rot=(0,0,1;0rad)
  Support = -> [XY_Plane043]
  expr: .AttachmentOffset.Base.y = -(<<Common>>#<<Parameters>>.boxsize_y / 2 - 20)
FEATURE [PartDesign::CoordinateSystem] Local_CS257  label="LCS_AFrame_PS_Corner_AS"
  AttacherType = Attacher::AttachEngine3D
  AttachmentOffset = pos=(10,103,0) rot=(0,0,-1;1.5708rad)
  MapMode = 5
  Placement = pos=(10,103,0) rot=(0,0,-1;1.5708rad)
  Support = -> [XY_Plane043]
  expr: .AttachmentOffset.Base.y = <<Common>>#<<Parameters>>.boxsize_y / 2 - 20
FEATURE [PartDesign::Body] Body029  label="AFrame_PS"
  Group = -> [Sketch048,Pad025,Local_CS104,Local_CS105,Local_CS,Local_CS257]
  Origin = -> Origin043
  Placement = pos=(113,0,-132) rot=(0,0,1;0rad)
  Tip = -> Pad025
  expr: .Placement.Base.x = <<Common>>#<<Parameters>>.bolt_x
  expr: .Placement.Base.z = <<Common>>#<<Parameters>>.datum_azbase
COMPONENT P20 — recipe-attached ("AFrame_AF", modeled in this document).
Construction recipe (the document's own serialized feature program — sketch geometry with constraints, then the solid features built on it; lengths are millimeters unless a unit is written):

FEATURE [PartDesign::CoordinateSystem] Local_CS223  label="LCS_AFrame_AF_BoltC"
  AttacherType = Attacher::AttachEngine3D
  MapMode = 5
  Placement = pos=(0,0,0) rot=(1,0,0;1.5708rad)
  Support = -> [XZ_Plane045]
FEATURE [Sketcher::SketchObject] Sketch049  label="AFrame_AF_Sketch"
  FullyConstrained = true
  MapMode = 5
  Placement = pos=(0,0,0) rot=(0.57735,0.57735,0.57735;2.0944rad)
  Support = -> [YZ_Plane045]
  sketch-geometry (75):
    g0: LineSegment StartX=3 StartY=10 StartZ=0 EndX=3 EndY=8 EndZ=0
    g1: LineSegment StartX=3 StartY=8 StartZ=0 EndX=6 EndY=8 EndZ=0
    g2: LineSegment StartX=2.58579 StartY=4 StartZ=0 EndX=-2.58579 EndY=4 EndZ=0
    g3: LineSegment StartX=-6 StartY=8 StartZ=0 EndX=-3 EndY=8 EndZ=0
    g4: LineSegment StartX=-3 StartY=8 StartZ=0 EndX=-3 EndY=10 EndZ=0
    g5: Circle CenterX=0 CenterY=0 CenterZ=0 NormalX=0 NormalY=0 NormalZ=1 AngleXU=0 Radius=2.1
    g6: LineSegment StartX=-10 StartY=3 StartZ=0 EndX=-8 EndY=3 EndZ=0
    g7: LineSegment StartX=-8 StartY=3 StartZ=0 EndX=-8 EndY=6 EndZ=0
    g8: LineSegment StartX=-4 StartY=2.58579 StartZ=0 EndX=-4 EndY=-2.58579 EndZ=0
    g9: LineSegment StartX=-8 StartY=-6 StartZ=0 EndX=-8 EndY=-3 EndZ=0
    g10: LineSegment StartX=-8 StartY=-3 StartZ=0 EndX=-10 EndY=-3 EndZ=0
    g11: LineSegment StartX=-3 StartY=-10 StartZ=0 EndX=-3 EndY=-8 EndZ=0
    g12: LineSegment StartX=-3 StartY=-8 StartZ=0 EndX=-6 EndY=-8 EndZ=0
    g13: LineSegment StartX=-2.58579 StartY=-4 StartZ=0 EndX=2.58579 EndY=-4 EndZ=0
    g14: LineSegment StartX=6 StartY=-8 StartZ=0 EndX=3 EndY=-8 EndZ=0
    g15: LineSegment StartX=3 StartY=-8 StartZ=0 EndX=3 EndY=-10 EndZ=0
    g16: LineSegment StartX=10 StartY=-3 StartZ=0 EndX=8 EndY=-3 EndZ=0
    g17: LineSegment StartX=8 StartY=-3 StartZ=0 EndX=8 EndY=-6 EndZ=0
    g18: LineSegment StartX=8 StartY=-6 StartZ=0 EndX=7.41421 EndY=-6 EndZ=0
    g19: LineSegment StartX=7.41421 StartY=-6 StartZ=0 EndX=4 EndY=-2.58579 EndZ=0
    g20: LineSegment StartX=4 StartY=-2.58579 StartZ=0 EndX=4 EndY=2.58579 EndZ=0
    g21: LineSegment StartX=4 StartY=2.58579 StartZ=0 EndX=7.41421 EndY=6 EndZ=0
    g22: LineSegment StartX=7.41421 StartY=6 StartZ=0 EndX=8 EndY=6 EndZ=0
    g23: LineSegment StartX=8 StartY=6 StartZ=0 EndX=8 EndY=3 EndZ=0
    g24: LineSegment StartX=8 StartY=3 StartZ=0 EndX=10 EndY=3 EndZ=0
    g25: LineSegment StartX=6 StartY=8 StartZ=0 EndX=6 EndY=7.41421 EndZ=0
    g26: LineSegment StartX=6 StartY=7.41421 StartZ=0 EndX=2.58579 EndY=4 EndZ=0
    g27: LineSegment StartX=-2.58579 StartY=4 StartZ=0 EndX=-6 EndY=7.41421 EndZ=0
    g28: LineSegment StartX=-6 StartY=7.41421 StartZ=0 EndX=-6 EndY=8 EndZ=0
    g29: LineSegment StartX=-8 StartY=6 StartZ=0 EndX=-7.41421 EndY=6 EndZ=0
    g30: LineSegment StartX=-7.41421 StartY=6 StartZ=0 EndX=-4 EndY=2.58579 EndZ=0
    g31: LineSegment StartX=-4 StartY=-2.58579 StartZ=0 EndX=-7.41421 EndY=-6 EndZ=0
    g32: LineSegment StartX=-7.41421 StartY=-6 StartZ=0 EndX=-8 EndY=-6 EndZ=0
    g33: LineSegment StartX=-2.58579 StartY=-4 StartZ=0 EndX=-6 EndY=-7.41421 EndZ=0
    g34: LineSegment StartX=-6 StartY=-7.41421 StartZ=0 EndX=-6 EndY=-8 EndZ=0
    g35: LineSegment StartX=2.58579 StartY=-4 StartZ=0 EndX=6 EndY=-7.41421 EndZ=0
    g36: LineSegment StartX=6 StartY=-7.41421 StartZ=0 EndX=6 EndY=-8 EndZ=0
    g37: LineSegment StartX=-4 StartY=2.58579 StartZ=0 EndX=-2.58579 EndY=4 EndZ=0
    g38: LineSegment StartX=-7.41421 StartY=7.41421 StartZ=0 EndX=7.41421 EndY=7.41421 EndZ=0
    g39: LineSegment StartX=7.41421 StartY=7.41421 StartZ=0 EndX=7.41421 EndY=-7.41421 EndZ=0
    g40: LineSegment StartX=7.41421 StartY=-7.41421 StartZ=0 EndX=-7.41421 EndY=-7.41421 EndZ=0
    g41: LineSegment StartX=-7.41421 StartY=-7.41421 StartZ=0 EndX=-7.41421 EndY=7.41421 EndZ=0
    g42: LineSegment StartX=-10 StartY=10 StartZ=0 EndX=10 EndY=10 EndZ=0
    g43: LineSegment StartX=10 StartY=10 StartZ=0 EndX=10 EndY=-10 EndZ=0
    g44: LineSegment StartX=10 StartY=-10 StartZ=0 EndX=-10 EndY=-10 EndZ=0
    g45: LineSegment StartX=-10 StartY=-10 StartZ=0 EndX=-10 EndY=10 EndZ=0
    g46: LineSegment StartX=4 StartY=4 StartZ=0 EndX=-4 EndY=4 EndZ=0
    g47: LineSegment StartX=-4 StartY=4 StartZ=0 EndX=-4 EndY=-4 EndZ=0
    g48: LineSegment StartX=-4 StartY=-4 StartZ=0 EndX=4 EndY=-4 EndZ=0
    g49: LineSegment StartX=4 StartY=-4 StartZ=0 EndX=4 EndY=4 EndZ=0
    g50: LineSegment StartX=-10 StartY=-10 StartZ=0 EndX=10 EndY=10 EndZ=0
    g51: LineSegment StartX=-10 StartY=10 StartZ=0 EndX=10 EndY=-10 EndZ=0
    g52: LineSegment StartX=2.58579 StartY=4 StartZ=0 EndX=4 EndY=2.58579 EndZ=0
    g53: LineSegment StartX=2.58579 StartY=-4 StartZ=0 EndX=4 EndY=-2.58579 EndZ=0
    g54: LineSegment StartX=-4 StartY=-2.58579 StartZ=0 EndX=-2.58579 EndY=-4 EndZ=0
    g55: LineSegment StartX=10 StartY=3 StartZ=0 EndX=3 EndY=10 EndZ=0
    g56: LineSegment StartX=-3 StartY=10 StartZ=0 EndX=-10 EndY=3 EndZ=0
    g57: LineSegment StartX=-10 StartY=-3 StartZ=0 EndX=-3 EndY=-10 EndZ=0
    g58: LineSegment StartX=3 StartY=-10 StartZ=0 EndX=10 EndY=-3 EndZ=0
    g59: ArcOfCircle CenterX=-9 CenterY=9 CenterZ=0 NormalX=0 NormalY=0 NormalZ=1 AngleXU=0 Radius=1 StartAngle=1.57078 EndAngle=3.14161
    g60: ArcOfCircle CenterX=9 CenterY=9 CenterZ=0 NormalX=0 NormalY=0 NormalZ=1 AngleXU=0 Radius=1 StartAngle=6.28316 EndAngle=7.854
    g61: ArcOfCircle CenterX=9 CenterY=-9 CenterZ=0 NormalX=0 NormalY=0 NormalZ=1 AngleXU=0 Radius=1 StartAngle=4.71238 EndAngle=6.28319
    g62: ArcOfCircle CenterX=-9 CenterY=-9 CenterZ=0 NormalX=0 NormalY=0 NormalZ=1 AngleXU=0 Radius=1 StartAngle=3.14159 EndAngle=4.71241
    g63: LineSegment StartX=-10 StartY=-9 StartZ=0 EndX=10 EndY=-9 EndZ=0
    g64: LineSegment StartX=-10 StartY=8.99998 StartZ=0 EndX=10 EndY=8.99998 EndZ=0
    g65: LineSegment StartX=-8.99998 StartY=10 StartZ=0 EndX=-8.99998 EndY=-10 EndZ=0
    g66: LineSegment StartX=8.99999 StartY=10 StartZ=0 EndX=8.99999 EndY=-10 EndZ=0
    g67: LineSegment StartX=-10 StartY=8.99998 StartZ=0 EndX=-10 EndY=3 EndZ=0
    g68: LineSegment StartX=-10 StartY=-3 StartZ=0 EndX=-10 EndY=-9 EndZ=0
    g69: LineSegment StartX=-8.99998 StartY=10 StartZ=0 EndX=-3 EndY=10 EndZ=0
    g70: LineSegment StartX=8.99999 StartY=10 StartZ=0 EndX=3 EndY=10 EndZ=0
    g71: LineSegment StartX=10 StartY=8.99998 StartZ=0 EndX=10 EndY=3 EndZ=0
    g72: LineSegment StartX=10 StartY=-9 StartZ=0 EndX=10 EndY=-3 EndZ=0
    g73: LineSegment StartX=8.99999 StartY=-10 StartZ=0 EndX=3 EndY=-10 EndZ=0
    g74: LineSegment StartX=-8.99998 StartY=-10 StartZ=0 EndX=-3 EndY=-10 EndZ=0
  constraints (212):
    c: Diameter(g5) = 4.2
    c: Coincident(g42,g43)
    c: Coincident(g43,g44)
    c: Coincident(g44,g45)
    c: Coincident(g45,g42)
    c: Horizontal(g44)
    c: Vertical(g45)
    c: Symmetric(g42,g43,g-1)
    c: Symmetric(g42,g42,g-2)
    c: Coincident(g5,g-1)
    c: Coincident(g38,g41)
    c: Coincident(g7,g29)
    c: Coincident(g29,g30)
    c: Coincident(g27,g28)
    c: Coincident(g3,g28)
    c: Coincident(g3,g4)
    c: Coincident(g6,g7)
    c: Coincident(g2,g27)
    c: Coincident(g2,g37)
    c: Coincident(g8,g30)
    c: Coincident(g8,g37)
    c: Coincident(g8,g31)
    c: Coincident(g13,g33)
    c: Coincident(g9,g10)
    c: Coincident(g11,g12)
    c: Coincident(g12,g34)
    c: Coincident(g33,g34)
    c: Coincident(g40,g41)
    c: Coincident(g31,g32)
    c: Coincident(g9,g32)
    c: Coincident(g14,g36)
    c: Coincident(g17,g18)
    c: Coincident(g39,g40)
    c: Coincident(g18,g19)
    c: Coincident(g35,g36)
    c: Coincident(g13,g35)
    c: Coincident(g19,g20)
    c: Coincident(g16,g17)
    c: Coincident(g0,g1)
    c: Coincident(g1,g25)
    c: Coincident(g22,g23)
    c: Coincident(g23,g24)
    c: Coincident(g21,g22)
    c: Coincident(g38,g39)
    c: Coincident(g25,g26)
    c: Coincident(g2,g26)
    c: Coincident(g20,g21)
    c: Horizontal(g1)
    c: Horizontal(g3)
    c: Horizontal(g12)
    c: Horizontal(g14)
    c: Vertical(g34)
    c: Vertical(g11)
    c: Vertical(g15)
    c: Vertical(g36)
    c: Vertical(g4)
    c: Vertical(g0)
    c: Vertical(g28)
    c: Vertical(g25)
    c: Vertical(g7)
    c: Vertical(g9)
    c: Vertical(g23)
    c: Vertical(g17)
    c: Horizontal(g29)
    c: Horizontal(g6)
    c: Horizontal(g10)
    c: Horizontal(g32)
    c: Horizontal(g22)
    c: Horizontal(g24)
    c: Horizontal(g16)
    c: Horizontal(g18)
    c: Parallel(g30,g27)
    c: Parallel(g27,g35)
    c: Parallel(g35,g19)
    c: Parallel(g21,g26)
    c: Parallel(g31,g33)
    c: Coincident(g46,g47)
    c: Coincident(g47,g48)
    c: Coincident(g48,g49)
    c: Coincident(g49,g46)
    c: Horizontal(g46)
    c: Horizontal(g48)
    c: Vertical(g47)
    c: Vertical(g49)
    c: Horizontal(g2)
    c: Horizontal(g13)
    c: Vertical(g8)
    c: Vertical(g20)
    c: PointOnObject(g2,g46)
    c: PointOnObject(g19,g49)
    c: PointOnObject(g13,g48)
    c: PointOnObject(g8,g47)
    c: Coincident(g50,g44)
    c: Coincident(g50,g42)
    c: Coincident(g51,g42)
    c: Coincident(g51,g43)
    c: PointOnObject(g39,g51)
    c: PointOnObject(g38,g50)
    c: PointOnObject(g38,g51)
    c: Vertical(g39)
    c: Vertical(g41)
    c: Horizontal(g38)
    c: Horizontal(g40)
    c: PointOnObject(g46,g50)
    c: PointOnObject(g46,g51)
    c: PointOnObject(g48,g51)
    c: Parallel(g27,g51)
    c: Parallel(g26,g50)
    c: Perpendicular(g51,g37)
    c: Parallel(g31,g26)
    c: PointOnObject(g4,g42)
    c: PointOnObject(g24,g43)
    c: PointOnObject(g6,g45)
    c: PointOnObject(g10,g45)
    c: PointOnObject(g29,g41)
    c: PointOnObject(g31,g41)
    c: PointOnObject(g33,g40)
    c: PointOnObject(g35,g40)
    c: PointOnObject(g18,g39)
    c: PointOnObject(g21,g39)
    c: PointOnObject(g25,g38)
    c: PointOnObject(g27,g38)
    c: Coincident(g52,g2)
    c: Coincident(g52,g20)
    c: Coincident(g53,g13)
    c: Coincident(g53,g19)
    c: Coincident(g54,g8)
    c: Coincident(g54,g13)
    c: Perpendicular(g50,g54)
    c: Perpendicular(g51,g53)
    c: Perpendicular(g50,g52)
    c: Equal(g37,g52)
    c: Equal(g52,g53)
    c: Equal(g53,g54)
    c: Distance(g37) = 2
    c: Coincident(g14,g15)
    c: PointOnObject(g6,g24)
    c: PointOnObject(g9,g16)
    c: PointOnObject(g11,g4)
    c: PointOnObject(g14,g0)
    c: PointOnObject(g11,g44)
    c: PointOnObject(g15,g44)
    c: DistanceX(g42) = 10
    c: DistanceY(g49,g49) = 8
    c: DistanceY(g18,g21) = 12
    c: Coincident(g56,g4)
    c: Coincident(g57,g10)
    c: Coincident(g58,g15)
    c: Perpendicular(g51,g58)
    c: Perpendicular(g50,g55)
    c: Perpendicular(g51,g56)
    c: Equal(g58,g57)
    c: Equal(g57,g55)
    c: DistanceY(g16,g24) = 6
    c: Equal(g42,g43)
    c: Coincident(g55,g0)
    c: Coincident(g55,g24)
    c: Coincident(g56,g6)
    c: Coincident(g11,g57)
    c: Coincident(g16,g58)
    c: DistanceX(g6,g6) = 2
    c: Equal(g6,g10)
    c: Equal(g10,g24)
    c: Equal(g24,g16)
    c: Equal(g16,g15)
    c: Equal(g15,g11)
    c: Equal(g11,g4)
    c: Equal(g4,g0)
    c: PointOnObject(g59,g51)
    c: PointOnObject(g59,g45)
    c: PointOnObject(g59,g42)
    c: PointOnObject(g60,g42)
    c: PointOnObject(g60,g43)
    c: PointOnObject(g61,g51)
    c: PointOnObject(g61,g43)
    c: PointOnObject(g61,g44)
    c: PointOnObject(g62,g50)
    c: PointOnObject(g62,g44)
    c: PointOnObject(g62,g45)
    c: Radius(g62) = 1
    c: Equal(g62,g59)
    c: Equal(g59,g60)
    c: Equal(g60,g61)
    c: Coincident(g63,g62)
    c: Coincident(g63,g61)
    c: Horizontal(g63)
    c: Coincident(g64,g59)
    c: Coincident(g64,g60)
    c: Horizontal(g64)
    c: Coincident(g65,g59)
    c: Coincident(g65,g62)
    c: Vertical(g65)
    c: Coincident(g66,g60)
    c: Coincident(g66,g61)
    c: Vertical(g66)
    c: PointOnObject(g62,g63)
    c: Coincident(g67,g59)
    c: Coincident(g67,g6)
    c: Coincident(g68,g10)
    c: Coincident(g68,g62)
    c: Coincident(g69,g59)
    c: Coincident(g69,g4)
    c: Coincident(g70,g60)
    c: Coincident(g70,g0)
    c: Coincident(g71,g60)
    c: Coincident(g71,g24)
    c: Coincident(g72,g61)
    c: Coincident(g72,g16)
    c: Coincident(g73,g61)
    c: Coincident(g73,g15)
    c: Coincident(g74,g62)
    c: Coincident(g74,g11)
FEATURE [PartDesign::Pad] Pad026  label="AFrame_AF_Pad"
  Direction = (1,-2e-16,3e-16)
  Length = 246
  Length2 = 100
  Midplane = true
  Placement = pos=(0,0,0) rot=(0.57735,0.57735,0.57735;2.0944rad)
  Profile = -> Sketch049
  Type = 0
  expr: Length = <<Common>>#<<Parameters>>.boxsize_x
FEATURE [Sketcher::SketchObject] Sketch058  label="AFrame_AF_Hole_Sketch"
  FullyConstrained = true
  MapMode = 5
  Placement = pos=(0,0,0) rot=(1,0,0;1.5708rad)
  Support = -> [XZ_Plane045]
  sketch-geometry (1):
    g0: Circle CenterX=0 CenterY=0 CenterZ=0 NormalX=0 NormalY=0 NormalZ=1 AngleXU=0 Radius=2.5
  constraints (2):
    c: Coincident(g0,g-1)
    c: Diameter(g0) = 5
FEATURE [PartDesign::Pocket] Pocket012  label="AFrame_AF_Hole"
  BaseFeature = -> Pad026
  Direction = (0,1,2e-16)
  Length = 5
  Length2 = 100
  Midplane = true
  Placement = pos=(0,0,0) rot=(0.57735,0.57735,0.57735;2.0944rad)
  Profile = -> Sketch058
  Type = 1
FEATURE [PartDesign::CoordinateSystem] Local_CS222  label="LCS_AFrame_AF_BoltS"
  AttacherType = Attacher::AttachEngine3D
  MapMode = 11
  Placement = pos=(-123,5.51e-14,-3.4e-14) rot=(0.707107,0,0.707107;3.14159rad)
  Support = -> [Pocket012]
FEATURE [PartDesign::CoordinateSystem] Local_CS221  label="LCS_AFrame_AF_BoltP"
  AttacherType = Attacher::AttachEngine3D
  MapMode = 11
  Placement = pos=(123,-5.42e-14,3.4e-14) rot=(0.707107,0,-0.707107;3.14159rad)
  Support = -> [Pocket012]
FEATURE [PartDesign::Body] Body031  label="AFrame_AF"
  Group = -> [Sketch049,Pad026,Sketch058,Pocket012,Local_CS221,Local_CS222,Local_CS223]
  Origin = -> Origin045
  Placement = pos=(0,113,-132) rot=(0,0,1;0rad)
  Tip = -> Pocket012
  expr: .Placement.Base.y = <<Common>>#<<Parameters>>.boxsize_y / 2 - 10
  expr: .Placement.Base.z = <<Common>>#<<Parameters>>.datum_azbase
COMPONENT P21 — recipe-attached ("AFrame_C", modeled in this document).
Construction recipe (the document's own serialized feature program — sketch geometry with constraints, then the solid features built on it; lengths are millimeters unless a unit is written):

FEATURE [Sketcher::SketchObject] Sketch056  label="AFrame_C_Sketch"
  FullyConstrained = true
  MapMode = 5
  Placement = pos=(0,0,0) rot=(1,0,0;1.5708rad)
  Support = -> [XZ_Plane049]
  sketch-geometry (75):
    g0: LineSegment StartX=3 StartY=10 StartZ=0 EndX=3 EndY=8 EndZ=0
    g1: LineSegment StartX=3 StartY=8 StartZ=0 EndX=6 EndY=8 EndZ=0
    g2: LineSegment StartX=2.58579 StartY=4 StartZ=0 EndX=-2.58579 EndY=4 EndZ=0
    g3: LineSegment StartX=-6 StartY=8 StartZ=0 EndX=-3 EndY=8 EndZ=0
    g4: LineSegment StartX=-3 StartY=8 StartZ=0 EndX=-3 EndY=10 EndZ=0
    g5: Circle CenterX=0 CenterY=0 CenterZ=0 NormalX=0 NormalY=0 NormalZ=1 AngleXU=0 Radius=2.1
    g6: LineSegment StartX=-10 StartY=3 StartZ=0 EndX=-8 EndY=3 EndZ=0
    g7: LineSegment StartX=-8 StartY=3 StartZ=0 EndX=-8 EndY=6 EndZ=0
    g8: LineSegment StartX=-4 StartY=2.58579 StartZ=0 EndX=-4 EndY=-2.58579 EndZ=0
    g9: LineSegment StartX=-8 StartY=-6 StartZ=0 EndX=-8 EndY=-3 EndZ=0
    g10: LineSegment StartX=-8 StartY=-3 StartZ=0 EndX=-10 EndY=-3 EndZ=0
    g11: LineSegment StartX=-3 StartY=-10 StartZ=0 EndX=-3 EndY=-8 EndZ=0
    g12: LineSegment StartX=-3 StartY=-8 StartZ=0 EndX=-6 EndY=-8 EndZ=0
    g13: LineSegment StartX=-2.58579 StartY=-4 StartZ=0 EndX=2.58579 EndY=-4 EndZ=0
    g14: LineSegment StartX=6 StartY=-8 StartZ=0 EndX=3 EndY=-8 EndZ=0
    g15: LineSegment StartX=3 StartY=-8 StartZ=0 EndX=3 EndY=-10 EndZ=0
    g16: LineSegment StartX=10 StartY=-3 StartZ=0 EndX=8 EndY=-3 EndZ=0
    g17: LineSegment StartX=8 StartY=-3 StartZ=0 EndX=8 EndY=-6 EndZ=0
    g18: LineSegment StartX=8 StartY=-6 StartZ=0 EndX=7.41421 EndY=-6 EndZ=0
    g19: LineSegment StartX=7.41421 StartY=-6 StartZ=0 EndX=4 EndY=-2.58579 EndZ=0
    g20: LineSegment StartX=4 StartY=-2.58579 StartZ=0 EndX=4 EndY=2.58579 EndZ=0
    g21: LineSegment StartX=4 StartY=2.58579 StartZ=0 EndX=7.41421 EndY=6 EndZ=0
    g22: LineSegment StartX=7.41421 StartY=6 StartZ=0 EndX=8 EndY=6 EndZ=0
    g23: LineSegment StartX=8 StartY=6 StartZ=0 EndX=8 EndY=3 EndZ=0
    g24: LineSegment StartX=8 StartY=3 StartZ=0 EndX=10 EndY=3 EndZ=0
    g25: LineSegment StartX=6 StartY=8 StartZ=0 EndX=6 EndY=7.41421 EndZ=0
    g26: LineSegment StartX=6 StartY=7.41421 StartZ=0 EndX=2.58579 EndY=4 EndZ=0
    g27: LineSegment StartX=-2.58579 StartY=4 StartZ=0 EndX=-6 EndY=7.41421 EndZ=0
    g28: LineSegment StartX=-6 StartY=7.41421 StartZ=0 EndX=-6 EndY=8 EndZ=0
    g29: LineSegment StartX=-8 StartY=6 StartZ=0 EndX=-7.41421 EndY=6 EndZ=0
    g30: LineSegment StartX=-7.41421 StartY=6 StartZ=0 EndX=-4 EndY=2.58579 EndZ=0
    g31: LineSegment StartX=-4 StartY=-2.58579 StartZ=0 EndX=-7.41421 EndY=-6 EndZ=0
    g32: LineSegment StartX=-7.41421 StartY=-6 StartZ=0 EndX=-8 EndY=-6 EndZ=0
    g33: LineSegment StartX=-2.58579 StartY=-4 StartZ=0 EndX=-6 EndY=-7.41421 EndZ=0
    g34: LineSegment StartX=-6 StartY=-7.41421 StartZ=0 EndX=-6 EndY=-8 EndZ=0
    g35: LineSegment StartX=2.58579 StartY=-4 StartZ=0 EndX=6 EndY=-7.41421 EndZ=0
    g36: LineSegment StartX=6 StartY=-7.41421 StartZ=0 EndX=6 EndY=-8 EndZ=0
    g37: LineSegment StartX=-4 StartY=2.58579 StartZ=0 EndX=-2.58579 EndY=4 EndZ=0
    g38: LineSegment StartX=-7.41421 StartY=7.41421 StartZ=0 EndX=7.41421 EndY=7.41421 EndZ=0
    g39: LineSegment StartX=7.41421 StartY=7.41421 StartZ=0 EndX=7.41421 EndY=-7.41421 EndZ=0
    g40: LineSegment StartX=7.41421 StartY=-7.41421 StartZ=0 EndX=-7.41421 EndY=-7.41421 EndZ=0
    g41: LineSegment StartX=-7.41421 StartY=-7.41421 StartZ=0 EndX=-7.41421 EndY=7.41421 EndZ=0
    g42: LineSegment StartX=-10 StartY=10 StartZ=0 EndX=10 EndY=10 EndZ=0
    g43: LineSegment StartX=10 StartY=10 StartZ=0 EndX=10 EndY=-10 EndZ=0
    g44: LineSegment StartX=10 StartY=-10 StartZ=0 EndX=-10 EndY=-10 EndZ=0
    g45: LineSegment StartX=-10 StartY=-10 StartZ=0 EndX=-10 EndY=10 EndZ=0
    g46: LineSegment StartX=4 StartY=4 StartZ=0 EndX=-4 EndY=4 EndZ=0
    g47: LineSegment StartX=-4 StartY=4 StartZ=0 EndX=-4 EndY=-4 EndZ=0
    g48: LineSegment StartX=-4 StartY=-4 StartZ=0 EndX=4 EndY=-4 EndZ=0
    g49: LineSegment StartX=4 StartY=-4 StartZ=0 EndX=4 EndY=4 EndZ=0
    g50: LineSegment StartX=-10 StartY=-10 StartZ=0 EndX=10 EndY=10 EndZ=0
    g51: LineSegment StartX=-10 StartY=10 StartZ=0 EndX=10 EndY=-10 EndZ=0
    g52: LineSegment StartX=2.58579 StartY=4 StartZ=0 EndX=4 EndY=2.58579 EndZ=0
    g53: LineSegment StartX=2.58579 StartY=-4 StartZ=0 EndX=4 EndY=-2.58579 EndZ=0
    g54: LineSegment StartX=-4 StartY=-2.58579 StartZ=0 EndX=-2.58579 EndY=-4 EndZ=0
    g55: LineSegment StartX=10 StartY=3 StartZ=0 EndX=3 EndY=10 EndZ=0
    g56: LineSegment StartX=-3 StartY=10 StartZ=0 EndX=-10 EndY=3 EndZ=0
    g57: LineSegment StartX=-10 StartY=-3 StartZ=0 EndX=-3 EndY=-10 EndZ=0
    g58: LineSegment StartX=3 StartY=-10 StartZ=0 EndX=10 EndY=-3 EndZ=0
    g59: ArcOfCircle CenterX=-9 CenterY=9 CenterZ=0 NormalX=0 NormalY=0 NormalZ=1 AngleXU=0 Radius=1 StartAngle=1.57078 EndAngle=3.14161
    g60: ArcOfCircle CenterX=9 CenterY=9 CenterZ=0 NormalX=0 NormalY=0 NormalZ=1 AngleXU=0 Radius=1 StartAngle=6.28316 EndAngle=7.854
    g61: ArcOfCircle CenterX=9 CenterY=-9 CenterZ=0 NormalX=0 NormalY=0 NormalZ=1 AngleXU=0 Radius=1 StartAngle=4.71238 EndAngle=6.28319
    g62: ArcOfCircle CenterX=-9 CenterY=-9 CenterZ=0 NormalX=0 NormalY=0 NormalZ=1 AngleXU=0 Radius=1 StartAngle=3.14159 EndAngle=4.71241
    g63: LineSegment StartX=-10 StartY=-9 StartZ=0 EndX=10 EndY=-9 EndZ=0
    g64: LineSegment StartX=-10 StartY=8.99998 StartZ=0 EndX=10 EndY=8.99998 EndZ=0
    g65: LineSegment StartX=-8.99998 StartY=10 StartZ=0 EndX=-8.99998 EndY=-10 EndZ=0
    g66: LineSegment StartX=8.99999 StartY=10 StartZ=0 EndX=8.99999 EndY=-10 EndZ=0
    g67: LineSegment StartX=-10 StartY=8.99998 StartZ=0 EndX=-10 EndY=3 EndZ=0
    g68: LineSegment StartX=-10 StartY=-3 StartZ=0 EndX=-10 EndY=-9 EndZ=0
    g69: LineSegment StartX=-8.99998 StartY=10 StartZ=0 EndX=-3 EndY=10 EndZ=0
    g70: LineSegment StartX=8.99999 StartY=10 StartZ=0 EndX=3 EndY=10 EndZ=0
    g71: LineSegment StartX=10 StartY=8.99998 StartZ=0 EndX=10 EndY=3 EndZ=0
    g72: LineSegment StartX=10 StartY=-9 StartZ=0 EndX=10 EndY=-3 EndZ=0
    g73: LineSegment StartX=8.99999 StartY=-10 StartZ=0 EndX=3 EndY=-10 EndZ=0
    g74: LineSegment StartX=-8.99998 StartY=-10 StartZ=0 EndX=-3 EndY=-10 EndZ=0
  constraints (212):
    c: Diameter(g5) = 4.2
    c: Coincident(g42,g43)
    c: Coincident(g43,g44)
    c: Coincident(g44,g45)
    c: Coincident(g45,g42)
    c: Horizontal(g44)
    c: Vertical(g45)
    c: Symmetric(g42,g43,g-1)
    c: Symmetric(g42,g42,g-2)
    c: Coincident(g5,g-1)
    c: Coincident(g38,g41)
    c: Coincident(g7,g29)
    c: Coincident(g29,g30)
    c: Coincident(g27,g28)
    c: Coincident(g3,g28)
    c: Coincident(g3,g4)
    c: Coincident(g6,g7)
    c: Coincident(g2,g27)
    c: Coincident(g2,g37)
    c: Coincident(g8,g30)
    c: Coincident(g8,g37)
    c: Coincident(g8,g31)
    c: Coincident(g13,g33)
    c: Coincident(g9,g10)
    c: Coincident(g11,g12)
    c: Coincident(g12,g34)
    c: Coincident(g33,g34)
    c: Coincident(g40,g41)
    c: Coincident(g31,g32)
    c: Coincident(g9,g32)
    c: Coincident(g14,g36)
    c: Coincident(g17,g18)
    c: Coincident(g39,g40)
    c: Coincident(g18,g19)
    c: Coincident(g35,g36)
    c: Coincident(g13,g35)
    c: Coincident(g19,g20)
    c: Coincident(g16,g17)
    c: Coincident(g0,g1)
    c: Coincident(g1,g25)
    c: Coincident(g22,g23)
    c: Coincident(g23,g24)
    c: Coincident(g21,g22)
    c: Coincident(g38,g39)
    c: Coincident(g25,g26)
    c: Coincident(g2,g26)
    c: Coincident(g20,g21)
    c: Horizontal(g1)
    c: Horizontal(g3)
    c: Horizontal(g12)
    c: Horizontal(g14)
    c: Vertical(g34)
    c: Vertical(g11)
    c: Vertical(g15)
    c: Vertical(g36)
    c: Vertical(g4)
    c: Vertical(g0)
    c: Vertical(g28)
    c: Vertical(g25)
    c: Vertical(g7)
    c: Vertical(g9)
    c: Vertical(g23)
    c: Vertical(g17)
    c: Horizontal(g29)
    c: Horizontal(g6)
    c: Horizontal(g10)
    c: Horizontal(g32)
    c: Horizontal(g22)
    c: Horizontal(g24)
    c: Horizontal(g16)
    c: Horizontal(g18)
    c: Parallel(g30,g27)
    c: Parallel(g27,g35)
    c: Parallel(g35,g19)
    c: Parallel(g21,g26)
    c: Parallel(g31,g33)
    c: Coincident(g46,g47)
    c: Coincident(g47,g48)
    c: Coincident(g48,g49)
    c: Coincident(g49,g46)
    c: Horizontal(g46)
    c: Horizontal(g48)
    c: Vertical(g47)
    c: Vertical(g49)
    c: Horizontal(g2)
    c: Horizontal(g13)
    c: Vertical(g8)
    c: Vertical(g20)
    c: PointOnObject(g2,g46)
    c: PointOnObject(g19,g49)
    c: PointOnObject(g13,g48)
    c: PointOnObject(g8,g47)
    c: Coincident(g50,g44)
    c: Coincident(g50,g42)
    c: Coincident(g51,g42)
    c: Coincident(g51,g43)
    c: PointOnObject(g39,g51)
    c: PointOnObject(g38,g50)
    c: PointOnObject(g38,g51)
    c: Vertical(g39)
    c: Vertical(g41)
    c: Horizontal(g38)
    c: Horizontal(g40)
    c: PointOnObject(g46,g50)
    c: PointOnObject(g46,g51)
    c: PointOnObject(g48,g51)
    c: Parallel(g27,g51)
    c: Parallel(g26,g50)
    c: Perpendicular(g51,g37)
    c: Parallel(g31,g26)
    c: PointOnObject(g4,g42)
    c: PointOnObject(g24,g43)
    c: PointOnObject(g6,g45)
    c: PointOnObject(g10,g45)
    c: PointOnObject(g29,g41)
    c: PointOnObject(g31,g41)
    c: PointOnObject(g33,g40)
    c: PointOnObject(g35,g40)
    c: PointOnObject(g18,g39)
    c: PointOnObject(g21,g39)
    c: PointOnObject(g25,g38)
    c: PointOnObject(g27,g38)
    c: Coincident(g52,g2)
    c: Coincident(g52,g20)
    c: Coincident(g53,g13)
    c: Coincident(g53,g19)
    c: Coincident(g54,g8)
    c: Coincident(g54,g13)
    c: Perpendicular(g50,g54)
    c: Perpendicular(g51,g53)
    c: Perpendicular(g50,g52)
    c: Equal(g37,g52)
    c: Equal(g52,g53)
    c: Equal(g53,g54)
    c: Distance(g37) = 2
    c: Coincident(g14,g15)
    c: PointOnObject(g6,g24)
    c: PointOnObject(g9,g16)
    c: PointOnObject(g11,g4)
    c: PointOnObject(g14,g0)
    c: PointOnObject(g11,g44)
    c: PointOnObject(g15,g44)
    c: DistanceX(g42) = 10
    c: DistanceY(g49,g49) = 8
    c: DistanceY(g18,g21) = 12
    c: Coincident(g56,g4)
    c: Coincident(g57,g10)
    c: Coincident(g58,g15)
    c: Perpendicular(g51,g58)
    c: Perpendicular(g50,g55)
    c: Perpendicular(g51,g56)
    c: Equal(g58,g57)
    c: Equal(g57,g55)
    c: DistanceY(g16,g24) = 6
    c: Equal(g42,g43)
    c: Coincident(g55,g0)
    c: Coincident(g55,g24)
    c: Coincident(g56,g6)
    c: Coincident(g11,g57)
    c: Coincident(g16,g58)
    c: DistanceX(g6,g6) = 2
    c: Equal(g6,g10)
    c: Equal(g10,g24)
    c: Equal(g24,g16)
    c: Equal(g16,g15)
    c: Equal(g15,g11)
    c: Equal(g11,g4)
    c: Equal(g4,g0)
    c: PointOnObject(g59,g51)
    c: PointOnObject(g59,g45)
    c: PointOnObject(g59,g42)
    c: PointOnObject(g60,g42)
    c: PointOnObject(g60,g43)
    c: PointOnObject(g61,g51)
    c: PointOnObject(g61,g43)
    c: PointOnObject(g61,g44)
    c: PointOnObject(g62,g50)
    c: PointOnObject(g62,g44)
    c: PointOnObject(g62,g45)
    c: Radius(g62) = 1
    c: Equal(g62,g59)
    c: Equal(g59,g60)
    c: Equal(g60,g61)
    c: Coincident(g63,g62)
    c: Coincident(g63,g61)
    c: Horizontal(g63)
    c: Coincident(g64,g59)
    c: Coincident(g64,g60)
    c: Horizontal(g64)
    c: Coincident(g65,g59)
    c: Coincident(g65,g62)
    c: Vertical(g65)
    c: Coincident(g66,g60)
    c: Coincident(g66,g61)
    c: Vertical(g66)
    c: PointOnObject(g62,g63)
    c: Coincident(g67,g59)
    c: Coincident(g67,g6)
    c: Coincident(g68,g10)
    c: Coincident(g68,g62)
    c: Coincident(g69,g59)
    c: Coincident(g69,g4)
    c: Coincident(g70,g60)
    c: Coincident(g70,g0)
    c: Coincident(g71,g60)
    c: Coincident(g71,g24)
    c: Coincident(g72,g61)
    c: Coincident(g72,g16)
    c: Coincident(g73,g61)
    c: Coincident(g73,g15)
    c: Coincident(g74,g62)
    c: Coincident(g74,g11)
FEATURE [PartDesign::Pad] Pad028  label="AFrame_C_Pad"
  Direction = (0,-1,-2e-16)
  Length = 206
  Length2 = 100
  Midplane = true
  Placement = pos=(0,0,0) rot=(1,0,0;1.5708rad)
  Profile = -> Sketch056
  Type = 0
  expr: Length = <<Common>>#<<Parameters>>.boxsize_y - 40
FEATURE [Sketcher::SketchObject] Sketch057  label="AFrame_C_Hole_Sketch"
  FullyConstrained = true
  MapMode = 5
  Placement = pos=(0,-9e-16,-4) rot=(1,0,0;3.14159rad)
  Support = -> [Pad028]
  sketch-geometry (1):
    g0: Circle CenterX=0 CenterY=0 CenterZ=0 NormalX=0 NormalY=0 NormalZ=1 AngleXU=0 Radius=4.4
  constraints (2):
    c: Diameter(g0) = 8.8
    c: Coincident(g0,g-1)
FEATURE [PartDesign::Pocket] Pocket011  label="AFrame_C_Hole"
  BaseFeature = -> Pad028
  Direction = (0,-2e-16,1)
  Length = 5
  Length2 = 100
  Midplane = true
  Placement = pos=(0,0,0) rot=(1,0,0;1.5708rad)
  Profile = -> Sketch057
  Type = 1
FEATURE [PartDesign::CoordinateSystem] Local_CS101  label="LCS_AFrame_C_BoltA"
  AttacherType = Attacher::AttachEngine3D
  MapMode = 11
  Placement = pos=(0,103,-2.29e-14) rot=(0.57735,-0.57735,-0.57735;4.18879rad)
  Support = -> [Pocket011]
FEATURE [PartDesign::CoordinateSystem] Local_CS102  label="LCS_AFrame_C_BoltF"
  AttacherType = Attacher::AttachEngine3D
  MapMode = 11
  Placement = pos=(0,-103,2.29e-14) rot=(0.57735,-0.57735,0.57735;2.0944rad)
  Support = -> [Pocket011]
FEATURE [PartDesign::CoordinateSystem] Local_CS219  label="LCS_AFrame_C_Pivot"
  AttacherType = Attacher::AttachEngine3D
  AttachmentOffset = pos=(0,0,215) rot=(0,0,1;0rad)
  MapMode = 5
  Placement = pos=(0,0,215) rot=(0,0,1;0rad)
  Support = -> [XY_Plane049]
  expr: .AttachmentOffset.Base.z = <<Common>>#<<Parameters>>.datum_rocker_z - <<Common>>#<<Parameters>>.datum_azbase
FEATURE [PartDesign::CoordinateSystem] Local_CS220  label="LCS_AFrame_C_BaseHub"
  AttacherType = Attacher::AttachEngine3D
  MapMode = 5
  Support = -> [XY_Plane049]
FEATURE [PartDesign::Body] Body035  label="AFrame_C"
  Group = -> [Sketch056,Pad028,Sketch057,Pocket011,Local_CS101,Local_CS102,Local_CS219,Local_CS220]
  Origin = -> Origin049
  Placement = pos=(0,0,-132) rot=(0,0,1;0rad)
  Tip = -> Pocket011
  expr: .Placement.Base.z = <<Common>>#<<Parameters>>.datum_azbase
PROVENANCE & LICENSES
A FreeCAD (.FCStd) document from a public repository crawl; recipes are the document's own serialized feature recipes (and, for linked parts, companion documents' recipes).
License: as declared in the source repository (recorded in the dataset sidecar).
